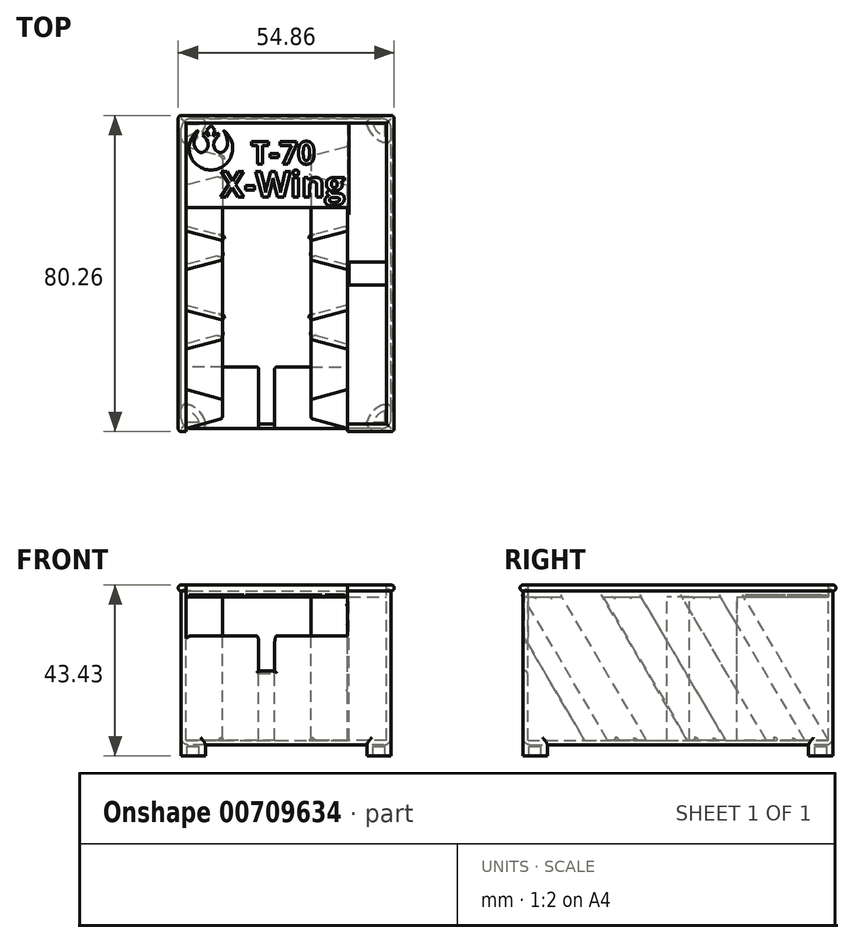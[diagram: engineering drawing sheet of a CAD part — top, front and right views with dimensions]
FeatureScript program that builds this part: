
annotation { "Feature Type Name" : "Feature", "Feature Type Description" : "" }
export const myFeature = defineFeature(function(context is Context, id is Id, definition is map)
    precondition{}
    {
        {
            var Q0;
            Q0=qCreatedBy(makeId("Front.planeOp"),FACE);
            var sketch = newSketch(context, id + "F0", { "sketchPlane" : qUnion([Q0])});
            skLineSegment(sketch, "E0.bottom", {"start": v(26.67, -20.32) * mm, "end": v(-26.67, -20.32) * mm});
            skLineSegment(sketch, "E0.top", {"start": v(26.67, 20.32) * mm, "end": v(-26.67, 20.32) * mm});
            skLineSegment(sketch, "E0.left", {"start": v(26.67, -20.32) * mm, "end": v(26.67, 20.32) * mm});
            skLineSegment(sketch, "E0.right", {"start": v(-26.67, -20.32) * mm, "end": v(-26.67, 20.32) * mm});
            skPoint(sketch, "E0.middle", {"position": v(0, 0) * mm});
            skSolve(sketch);
        }
        {
            var Q0;
            Q0=qSketchRegion(id+"F0",true);
            extrude(context, id + "F1", {"entities" : qUnion([Q0]), "depth" : 78.74 * mm, "offsetDistance" : 25.4 * mm, "symmetric" : true});
        }
        {
            var Q0;
            Q0=makeQuery(id+"F1.opExtrude","SWEPT_FACE",FACE,{"disambiguationData":[OSD([sQuery(id+"F0.wireOp",EDGE,"E0.top")])]});
            shell(context, id + "F2", {"entities" : qUnion([Q0]), "thickness" : 1.2 * mm});
        }
        {
            var Q0;
            {var subQ0=sQuery(id+"F0.wireOp",EDGE,"E0.right");var subQ3=sQuery(id+"F0.wireOp",EDGE,"E0.top");Q0=makeQuery(id+"F15.boolean.opBoolean","SPLIT",EDGE,{"disambiguationData":[TD([makeQuery(id+"F2.opShell","OFFSET_FACE",FACE,{"disambiguationData":[OSD([subQ0])]})])],"derivedFrom":makeQuery(id+"F2.opShell","OFFSET_EDGE",EDGE,{"disambiguationData":[OSD([subQ3]),TDD([makeQuery(id+"F1.opExtrude","CAP_EDGE",EDGE,{"disambiguationData":[OSD([subQ3])],"isStart":false})])]})});}
            var Q1;
            {var subQ0=sQuery(id+"F6.wireOp",EDGE,"E8");var subQ1=sQuery(id+"F0.wireOp",EDGE,"E0.right");var subQ2=sQuery(id+"F0.wireOp",EDGE,"E0.top");var subQ3=makeQuery(id+"F1.opExtrude","CAP_EDGE",EDGE,{"disambiguationData":[OSD([subQ2])],"isStart":false});Q1=makeQuery(id+"F7.boolean.opBoolean","MERGE",EDGE,{"derivedFrom":[subQ3,makeQuery(id+"F7.opSweep","SWEPT_EDGE",EDGE,{"disambiguationData":[OSD([subQ2,subQ1,subQ0]),TDD([subQ3,makeQuery(id+"F6.imprint","INTERSECT",VERTEX,{"derivedFrom":[subQ3,makeQuery(id+"F1.opExtrude","CAP_EDGE",EDGE,{"disambiguationData":[OSD([subQ1])],"isStart":false}),subQ0]})])]})]});}
            cPlane(context, id + "F3", {"entities" : qUnion([Q0, Q1]), "cplaneType" : CPlaneType.LINE_ANGLE, "offset" : 25.4 * mm, "angle" : 30.5 * degree, "oppositeDirection" : true, "width" : 152.4 * mm, "height" : 152.4 * mm});
        }
        {
            var Q0;
            Q0=makeQuery(id+"F2.opShell","OFFSET_FACE",FACE,{"disambiguationData":[OSD([sQuery(id+"F0.wireOp",EDGE,"E0.right")])]});
            var sketch = newSketch(context, id + "F4", { "sketchPlane" : qUnion([Q0])});
            skLineSegment(sketch, "E1.0", {"start": v(38.17, -19.12) * mm, "end": v(38.17, 20.32) * mm});
            skLineSegment(sketch, "E2.1", {"start": v(-38.17, -19.12) * mm, "end": v(38.17, -19.12) * mm});
            skLineSegment(sketch, "E3", {"start": v(38.17, -19.12) * mm, "end": v(-5.73, 55.41) * mm});
            skLineSegment(sketch, "E4.0", {"start": v(-38.17, 20.32) * mm, "end": v(38.17, 20.32) * mm});
            skPoint(sketch, "E5", {"position": v(14.94, 20.32) * mm});
            skSolve(sketch);
        }
        {
            var Q0;
            Q0=qCreatedBy(id+"F3.planeOp",FACE);
            var sketch = newSketch(context, id + "F5", { "sketchPlane" : qUnion([Q0])});
            skPoint(sketch, "E6.0", {"position": v(-25.47, 23.18) * mm});
            skSolve(sketch);
        }
        {
            var Q0;
            Q0=makeQuery(id+"F1.opExtrude","CAP_FACE",FACE,{"disambiguationData":[OSD([sQuery(id+"F0.wireOp",EDGE,"E0.bottom"),sQuery(id+"F0.wireOp",EDGE,"E0.top"),sQuery(id+"F0.wireOp",EDGE,"E0.left"),sQuery(id+"F0.wireOp",EDGE,"E0.right")])],"isStart":false});
            var sketch = newSketch(context, id + "F6", { "sketchPlane" : qUnion([Q0])});
            skArc(sketch, "E7", {"start": v(-122.9, 118.26) * mm, "mid": v(-123.67, 117.5) * mm, "end": v(-122.9, 116.74) * mm});
            skArc(sketch, "E8", {"start": v(-26.67, 20.32) * mm, "mid": v(-27.43, 19.56) * mm, "end": v(-26.67, 18.8) * mm});
            skSolve(sketch);
        }
        {
            var Q0;
            {var subQ0=sQuery(id+"F6.wireOp",EDGE,"E8");Q0=makeQuery(id+"F6.imprint","IMPRINT",FACE,{"disambiguationData":[TD([[makeQuery(id+"F6.imprint","IMPRINT",EDGE,{"derivedFrom":subQ0}),1.0]])]});}
            var Q1;
            Q1=makeQuery(id+"F1.opExtrude","CAP_EDGE",EDGE,{"disambiguationData":[OSD([sQuery(id+"F0.wireOp",EDGE,"E0.top")])],"isStart":false});
            var Q2;
            Q2=makeQuery(id+"F1.opExtrude","SWEPT_EDGE",EDGE,{"disambiguationData":[OSD([sQuery(id+"F0.wireOp",EDGE,"E0.top"),sQuery(id+"F0.wireOp",EDGE,"E0.right")])]});
            var Q3;
            Q3=makeQuery(id+"F1.opExtrude","SWEPT_EDGE",EDGE,{"disambiguationData":[OSD([sQuery(id+"F0.wireOp",EDGE,"E0.top"),sQuery(id+"F0.wireOp",EDGE,"E0.left")])]});
            var Q4;
            Q4=makeQuery(id+"F1.opExtrude","CAP_EDGE",EDGE,{"disambiguationData":[OSD([sQuery(id+"F0.wireOp",EDGE,"E0.top")])],"isStart":true});
            sweep(context, id + "F7", {"operationType" : NewBodyOperationType.ADD, "profiles" : qUnion([Q0]), "path" : qUnion([Q1, Q2, Q3, Q4])});
        }
        {
            var Q0;
            Q0=makeQuery(id+"F1.opExtrude","SWEPT_FACE",FACE,{"disambiguationData":[OSD([sQuery(id+"F0.wireOp",EDGE,"E0.bottom")])]});
            var sketch = newSketch(context, id + "F8", { "sketchPlane" : qUnion([Q0])});
            skLineSegment(sketch, "E9.bottom", {"start": v(26.67, 39.37) * mm, "end": v(21.75, 39.37) * mm});
            skLineSegment(sketch, "E9.left", {"start": v(26.67, 39.37) * mm, "end": v(26.67, 34.45) * mm});
            skPoint(sketch, "E10.newPointA", {"position": v(20.32, 19.05) * mm});
            skArc(sketch, "E11", {"start": v(20.52, 37.78) * mm, "mid": v(22.18, 34.88) * mm, "end": v(25.08, 33.22) * mm});
            skPoint(sketch, "E12.visualSharp", {"position": v(20.32, 39.37) * mm});
            skArc(sketch, "E12.filletArc", {"start": v(21.75, 39.37) * mm, "mid": v(20.75, 38.88) * mm, "end": v(20.52, 37.78) * mm});
            skPoint(sketch, "E13.visualSharp", {"position": v(26.67, 33.02) * mm});
            skArc(sketch, "E13.filletArc", {"start": v(25.08, 33.22) * mm, "mid": v(26.18, 33.45) * mm, "end": v(26.67, 34.45) * mm});
            skArc(sketch, "E14.MirrorCS", {"start": v(-21.75, 39.37) * mm, "mid": v(-20.75, 38.88) * mm, "end": v(-20.52, 37.78) * mm});
            skArc(sketch, "E15.MirrorCS", {"start": v(-20.52, 37.78) * mm, "mid": v(-22.18, 34.88) * mm, "end": v(-25.08, 33.22) * mm});
            skArc(sketch, "E16.MirrorCS", {"start": v(-25.08, 33.22) * mm, "mid": v(-26.18, 33.45) * mm, "end": v(-26.67, 34.45) * mm});
            skLineSegment(sketch, "E17.MirrorCS", {"start": v(-26.67, 39.37) * mm, "end": v(-26.67, 34.45) * mm});
            skLineSegment(sketch, "E18.MirrorCS", {"start": v(-26.67, 39.37) * mm, "end": v(-21.75, 39.37) * mm});
            skArc(sketch, "E19.MirrorCS", {"start": v(-20.52, -37.78) * mm, "mid": v(-22.18, -34.88) * mm, "end": v(-25.08, -33.22) * mm});
            skArc(sketch, "E20.MirrorCS", {"start": v(-21.75, -39.37) * mm, "mid": v(-20.75, -38.88) * mm, "end": v(-20.52, -37.78) * mm});
            skLineSegment(sketch, "E21.MirrorCS", {"start": v(-26.67, -39.37) * mm, "end": v(-21.75, -39.37) * mm});
            skLineSegment(sketch, "E22.MirrorCS", {"start": v(-26.67, -39.37) * mm, "end": v(-26.67, -34.45) * mm});
            skArc(sketch, "E23.MirrorCS", {"start": v(-25.08, -33.22) * mm, "mid": v(-26.18, -33.45) * mm, "end": v(-26.67, -34.45) * mm});
            skArc(sketch, "E24.MirrorCS", {"start": v(21.75, -39.37) * mm, "mid": v(20.75, -38.88) * mm, "end": v(20.52, -37.78) * mm});
            skArc(sketch, "E25.MirrorCS", {"start": v(20.52, -37.78) * mm, "mid": v(22.18, -34.88) * mm, "end": v(25.08, -33.22) * mm});
            skArc(sketch, "E26.MirrorCS", {"start": v(25.08, -33.22) * mm, "mid": v(26.18, -33.45) * mm, "end": v(26.67, -34.45) * mm});
            skLineSegment(sketch, "E27.MirrorCS", {"start": v(26.67, -39.37) * mm, "end": v(26.67, -34.45) * mm});
            skLineSegment(sketch, "E28.MirrorCS", {"start": v(26.67, -39.37) * mm, "end": v(21.75, -39.37) * mm});
            skSolve(sketch);
        }
        {
            var Q0;
            Q0=qSketchRegion(id+"F8",true);
            extrude(context, id + "F9", {"entities" : qUnion([Q0]), "operationType" : NewBodyOperationType.ADD, "depth" : 2.8 * mm, "offsetDistance" : 25.4 * mm});
        }
        {
            var Q0;
            Q0=makeQuery(id+"F9.opExtrude","CAP_FACE",FACE,{"disambiguationData":[OSD([sQuery(id+"F8.wireOp",EDGE,"E15.MirrorCS"),sQuery(id+"F8.wireOp",EDGE,"E16.MirrorCS"),sQuery(id+"F8.wireOp",EDGE,"E17.MirrorCS"),sQuery(id+"F8.wireOp",EDGE,"E14.MirrorCS"),sQuery(id+"F8.wireOp",EDGE,"E18.MirrorCS")])],"isStart":false});
            var Q1;
            Q1=makeQuery(id+"F9.opExtrude","CAP_FACE",FACE,{"disambiguationData":[OSD([sQuery(id+"F8.wireOp",EDGE,"E9.bottom"),sQuery(id+"F8.wireOp",EDGE,"E9.left"),sQuery(id+"F8.wireOp",EDGE,"E11"),sQuery(id+"F8.wireOp",EDGE,"E12.filletArc"),sQuery(id+"F8.wireOp",EDGE,"E13.filletArc")])],"isStart":false});
            var Q2;
            Q2=makeQuery(id+"F9.opExtrude","CAP_FACE",FACE,{"disambiguationData":[OSD([sQuery(id+"F8.wireOp",EDGE,"E24.MirrorCS"),sQuery(id+"F8.wireOp",EDGE,"E25.MirrorCS"),sQuery(id+"F8.wireOp",EDGE,"E26.MirrorCS"),sQuery(id+"F8.wireOp",EDGE,"E27.MirrorCS"),sQuery(id+"F8.wireOp",EDGE,"E28.MirrorCS")])],"isStart":false});
            var Q3;
            Q3=makeQuery(id+"F9.opExtrude","CAP_FACE",FACE,{"disambiguationData":[OSD([sQuery(id+"F8.wireOp",EDGE,"E19.MirrorCS"),sQuery(id+"F8.wireOp",EDGE,"E20.MirrorCS"),sQuery(id+"F8.wireOp",EDGE,"E21.MirrorCS"),sQuery(id+"F8.wireOp",EDGE,"E22.MirrorCS"),sQuery(id+"F8.wireOp",EDGE,"E23.MirrorCS")])],"isStart":false});
            shell(context, id + "F10", {"entities" : qUnion([Q0, Q1, Q2, Q3]), "thickness" : 1.52 * mm});
        }
        {
            var Q0;
            Q0=makeQuery(id+"F7.opSweep","MID_CAP_EDGE",EDGE,{"disambiguationData":[OSD([sQuery(id+"F0.wireOp",EDGE,"E0.top"),sQuery(id+"F0.wireOp",EDGE,"E0.right"),sQuery(id+"F6.wireOp",EDGE,"E8")])],"capPos":1.0});
            var Q1;
            Q1=makeQuery(id+"F7.opSweep","CAP_EDGE",EDGE,{"disambiguationData":[OSD([sQuery(id+"F0.wireOp",EDGE,"E0.top"),sQuery(id+"F0.wireOp",EDGE,"E0.right"),sQuery(id+"F6.wireOp",EDGE,"E8")])],"isStart":true});
            var Q2;
            Q2=makeQuery(id+"F7.opSweep","MID_CAP_EDGE",EDGE,{"disambiguationData":[OSD([sQuery(id+"F0.wireOp",EDGE,"E0.top"),sQuery(id+"F0.wireOp",EDGE,"E0.left"),sQuery(id+"F6.wireOp",EDGE,"E8")])],"capPos":3.0});
            var Q3;
            Q3=makeQuery(id+"F7.opSweep","MID_CAP_EDGE",EDGE,{"disambiguationData":[OSD([sQuery(id+"F0.wireOp",EDGE,"E0.top"),sQuery(id+"F0.wireOp",EDGE,"E0.left"),sQuery(id+"F6.wireOp",EDGE,"E8")])],"capPos":2.0});
            fillet(context, id + "F11", {"entities" : qUnion([Q0, Q1, Q2, Q3]), "radius" : 0.76 * mm, "tangentPropagation" : true, "allowEdgeOverflow" : false});
        }
        {
            var Q0;
            Q0=makeQuery(id+"F9.boolean.opBoolean","MERGE",EDGE,{"derivedFrom":[makeQuery(id+"F1.opExtrude","CAP_EDGE",EDGE,{"disambiguationData":[OSD([sQuery(id+"F0.wireOp",EDGE,"E0.right")])],"isStart":false}),makeQuery(id+"F9.opExtrude","SWEPT_EDGE",EDGE,{"disambiguationData":[OSD([sQuery(id+"F8.wireOp",EDGE,"E17.MirrorCS"),sQuery(id+"F8.wireOp",EDGE,"E18.MirrorCS")])]})]});
            var Q1;
            Q1=makeQuery(id+"F9.boolean.opBoolean","MERGE",EDGE,{"derivedFrom":[makeQuery(id+"F1.opExtrude","CAP_EDGE",EDGE,{"disambiguationData":[OSD([sQuery(id+"F0.wireOp",EDGE,"E0.left")])],"isStart":false}),makeQuery(id+"F9.opExtrude","SWEPT_EDGE",EDGE,{"disambiguationData":[OSD([sQuery(id+"F8.wireOp",EDGE,"E9.bottom"),sQuery(id+"F8.wireOp",EDGE,"E9.left")])]})]});
            var Q2;
            Q2=makeQuery(id+"F9.boolean.opBoolean","MERGE",EDGE,{"derivedFrom":[makeQuery(id+"F1.opExtrude","CAP_EDGE",EDGE,{"disambiguationData":[OSD([sQuery(id+"F0.wireOp",EDGE,"E0.left")])],"isStart":true}),makeQuery(id+"F9.opExtrude","SWEPT_EDGE",EDGE,{"disambiguationData":[OSD([sQuery(id+"F8.wireOp",EDGE,"E27.MirrorCS"),sQuery(id+"F8.wireOp",EDGE,"E28.MirrorCS")])]})]});
            var Q3;
            Q3=makeQuery(id+"F9.boolean.opBoolean","MERGE",EDGE,{"derivedFrom":[makeQuery(id+"F1.opExtrude","CAP_EDGE",EDGE,{"disambiguationData":[OSD([sQuery(id+"F0.wireOp",EDGE,"E0.right")])],"isStart":true}),makeQuery(id+"F9.opExtrude","SWEPT_EDGE",EDGE,{"disambiguationData":[OSD([sQuery(id+"F8.wireOp",EDGE,"E21.MirrorCS"),sQuery(id+"F8.wireOp",EDGE,"E22.MirrorCS")])]})]});
            fillet(context, id + "F12", {"entities" : qUnion([Q0, Q1, Q2, Q3]), "radius" : 2.54 * mm, "tangentPropagation" : true, "allowEdgeOverflow" : false});
        }
        {
            var Q0;
            Q0=makeQuery(id+"F1.opExtrude","SWEPT_EDGE",EDGE,{"disambiguationData":[OSD([sQuery(id+"F0.wireOp",EDGE,"E0.bottom"),sQuery(id+"F0.wireOp",EDGE,"E0.right")])]});
            var Q1;
            Q1=makeQuery(id+"F1.opExtrude","CAP_EDGE",EDGE,{"disambiguationData":[OSD([sQuery(id+"F0.wireOp",EDGE,"E0.bottom")])],"isStart":false});
            var Q2;
            Q2=makeQuery(id+"F1.opExtrude","SWEPT_EDGE",EDGE,{"disambiguationData":[OSD([sQuery(id+"F0.wireOp",EDGE,"E0.bottom"),sQuery(id+"F0.wireOp",EDGE,"E0.left")])]});
            var Q3;
            Q3=makeQuery(id+"F1.opExtrude","CAP_EDGE",EDGE,{"disambiguationData":[OSD([sQuery(id+"F0.wireOp",EDGE,"E0.bottom")])],"isStart":true});
            fillet(context, id + "F13", {"entities" : qUnion([Q0, Q1, Q2, Q3]), "radius" : 1.9 * mm, "tangentPropagation" : true, "allowEdgeOverflow" : false});
        }
        {
            var Q0;
            Q0=makeQuery(id+"F23.boolean.opBoolean","MERGE",FACE,{"derivedFrom":[makeQuery(id+"F1.opExtrude","SWEPT_FACE",FACE,{"disambiguationData":[OSD([sQuery(id+"F0.wireOp",EDGE,"E0.top")])]}),makeQuery(id+"F23.opExtrude","CAP_FACE",FACE,{"disambiguationData":[OSD([sQuery(id+"F22.wireOp",EDGE,"CeT5EqMD-vzeh-J7pB-LkoM-5uFaC58c3kCY.bottom"),sQuery(id+"F22.wireOp",EDGE,"CeT5EqMD-vzeh-J7pB-LkoM-5uFaC58c3kCY.top"),sQuery(id+"F22.wireOp",EDGE,"CeT5EqMD-vzeh-J7pB-LkoM-5uFaC58c3kCY.left"),sQuery(id+"F22.wireOp",EDGE,"CeT5EqMD-vzeh-J7pB-LkoM-5uFaC58c3kCY.right")])],"isStart":true})]});
            var sketch = newSketch(context, id + "F14", { "sketchPlane" : qUnion([Q0])});
            skLineSegment(sketch, "E29.bottom", {"start": v(25.47, 38.17) * mm, "end": v(15.93, 38.17) * mm});
            skLineSegment(sketch, "E29.top", {"start": v(25.47, 2.86) * mm, "end": v(15.93, 2.86) * mm});
            skLineSegment(sketch, "E29.left", {"start": v(25.47, 38.17) * mm, "end": v(25.47, 2.86) * mm});
            skLineSegment(sketch, "E29.right", {"start": v(15.93, 38.17) * mm, "end": v(15.93, 2.86) * mm});
            skLineSegment(sketch, "E30.bottom", {"start": v(25.47, -38.17) * mm, "end": v(15.93, -38.17) * mm});
            skLineSegment(sketch, "E30.top", {"start": v(25.47, -2.86) * mm, "end": v(15.93, -2.86) * mm});
            skLineSegment(sketch, "E30.left", {"start": v(25.47, -38.17) * mm, "end": v(25.47, -2.86) * mm});
            skLineSegment(sketch, "E30.right", {"start": v(15.93, -38.17) * mm, "end": v(15.93, -2.86) * mm});
            skLineSegment(sketch, "E31.bottom", {"start": v(25.47, 38.17) * mm, "end": v(-25.47, 38.17) * mm});
            skLineSegment(sketch, "E31.top", {"start": v(25.47, -38.17) * mm, "end": v(-25.47, -38.17) * mm});
            skLineSegment(sketch, "E31.left", {"start": v(25.47, 38.17) * mm, "end": v(25.47, -38.17) * mm});
            skLineSegment(sketch, "E31.right", {"start": v(-25.47, 38.17) * mm, "end": v(-25.47, -38.17) * mm});
            skLineSegment(sketch, "E32", {"start": v(15.93, -38.17) * mm, "end": v(15.93, -38.17) * mm});
            skLineSegment(sketch, "E33", {"start": v(15.93, -38.17) * mm, "end": v(15.93, 38.17) * mm});
            skLineSegment(sketch, "E34.0", {"start": v(-25.47, 38.17) * mm, "end": v(-25.47, -5.73) * mm});
            skPoint(sketch, "E35.0", {"position": v(-25.47, 14.94) * mm});
            skLineSegment(sketch, "E36", {"start": v(-25.47, 14.94) * mm, "end": v(15.93, 14.94) * mm});
            skSolve(sketch);
        }
        {
            var Q0;
            {var subQ3=sQuery(id+"F14.wireOp",EDGE,"E29.top");Q0=makeQuery(id+"F14.imprint","IMPRINT",FACE,{"disambiguationData":[TD([[makeQuery(id+"F14.imprint","IMPRINT",EDGE,{"derivedFrom":subQ3}),1.0]])]});}
            var Q1;
            {var subQ5=sQuery(id+"F14.wireOp",EDGE,"E36");Q1=makeQuery(id+"F14.imprint","IMPRINT",FACE,{"disambiguationData":[TD([[makeQuery(id+"F14.imprint","IMPRINT",EDGE,{"derivedFrom":subQ5}),1.0]])]});}
            var Q2;
            Q2=makeQuery(id+"F2.opShell","OFFSET_FACE",FACE,{"disambiguationData":[OSD([sQuery(id+"F0.wireOp",EDGE,"E0.bottom")])]});
            extrude(context, id + "F15", {"entities" : qUnion([Q0, Q1]), "operationType" : NewBodyOperationType.ADD, "endBound" : BoundingType.UP_TO_SURFACE, "oppositeDirection" : true, "depth" : 25.4 * mm, "endBoundEntityFace" : qUnion([Q2]), "offsetDistance" : 25.4 * mm});
        }
        {
            var Q0;
            Q0=qCreatedBy(id+"F3.planeOp",FACE);
            var sketch = newSketch(context, id + "F16", { "sketchPlane" : qUnion([Q0])});
            skLineSegment(sketch, "E37.0", {"start": v(-25.47, -16.63) * mm, "end": v(-25.47, -7.74) * mm});
            skLineSegment(sketch, "E38", {"start": v(-25.47, 23.18) * mm, "end": v(-4.77, 23.18) * mm});
            skPoint(sketch, "E39.0", {"position": v(-25.47, 23.18) * mm});
            skLineSegment(sketch, "E40", {"start": v(-25.47, 23.18) * mm, "end": v(-25.47, 18.1) * mm});
            skLineSegment(sketch, "E41", {"start": v(-25.47, 18.1) * mm, "end": v(-16.19, 15.96) * mm});
            skLineSegment(sketch, "E42", {"start": v(-16.19, 15.96) * mm, "end": v(-16.19, 11.77) * mm});
            skLineSegment(sketch, "E43", {"start": v(-16.19, 11.77) * mm, "end": v(-25.47, 9.63) * mm});
            skLineSegment(sketch, "E44", {"start": v(-25.47, 9.63) * mm, "end": v(-25.47, 0.74) * mm});
            skLineSegment(sketch, "E45", {"start": v(-25.47, 0.74) * mm, "end": v(-16.19, -1.4) * mm});
            skLineSegment(sketch, "E46", {"start": v(-16.19, -1.4) * mm, "end": v(-16.19, -5.6) * mm});
            skLineSegment(sketch, "E47", {"start": v(-16.19, -5.6) * mm, "end": v(-25.47, -7.74) * mm});
            skLineSegment(sketch, "E48", {"start": v(-25.47, -7.74) * mm, "end": v(-25.47, -16.63) * mm});
            skLineSegment(sketch, "E49", {"start": v(-25.47, -16.63) * mm, "end": v(-16.19, -18.77) * mm});
            skLineSegment(sketch, "E50", {"start": v(-16.19, -18.77) * mm, "end": v(-16.19, -22.96) * mm});
            skLineSegment(sketch, "E51", {"start": v(-16.19, -22.96) * mm, "end": v(-25.47, -25.1) * mm});
            skLineSegment(sketch, "E52", {"start": v(-25.47, -25.1) * mm, "end": v(-25.47, -30.18) * mm});
            skLineSegment(sketch, "E53", {"start": v(-25.47, -30.18) * mm, "end": v(-7, -30.18) * mm});
            skLineSegment(sketch, "E54", {"start": v(-7, -30.18) * mm, "end": v(-7, -34) * mm});
            skLineSegment(sketch, "E55", {"start": v(-7, -34) * mm, "end": v(-4.77, -34) * mm});
            skLineSegment(sketch, "E56.trimOffspring", {"start": v(-25.47, 0.74) * mm, "end": v(-25.47, 9.63) * mm});
            skLineSegment(sketch, "E57.trimOffspring", {"start": v(-25.47, 18.1) * mm, "end": v(-25.47, 23.18) * mm});
            skPoint(sketch, "E58.orphan", {"position": v(-25.47, -22.58) * mm});
            skLineSegment(sketch, "E59", {"start": v(-4.95, -94.16) * mm, "end": v(-4.95, 57.75) * mm});
            skLineSegment(sketch, "E60.MirrorCS", {"start": v(15.56, 23.18) * mm, "end": v(15.56, 18.1) * mm});
            skLineSegment(sketch, "E61.MirrorCS", {"start": v(6.28, -1.4) * mm, "end": v(6.28, -5.6) * mm});
            skLineSegment(sketch, "E62.MirrorCS", {"start": v(-2.91, -34) * mm, "end": v(-5.14, -34) * mm});
            skLineSegment(sketch, "E63.MirrorCS", {"start": v(15.56, 18.1) * mm, "end": v(15.56, 23.18) * mm});
            skLineSegment(sketch, "E64.MirrorCS", {"start": v(6.28, 15.96) * mm, "end": v(6.28, 11.77) * mm});
            skLineSegment(sketch, "E65.MirrorCS", {"start": v(6.28, -18.77) * mm, "end": v(6.28, -22.96) * mm});
            skLineSegment(sketch, "E66.MirrorCS", {"start": v(15.56, -16.63) * mm, "end": v(15.56, -7.74) * mm});
            skLineSegment(sketch, "E67.MirrorCS", {"start": v(-2.91, -30.18) * mm, "end": v(-2.91, -34) * mm});
            skLineSegment(sketch, "E68.MirrorCS", {"start": v(15.56, 18.1) * mm, "end": v(6.28, 15.96) * mm});
            skLineSegment(sketch, "E69.MirrorCS", {"start": v(6.28, 11.77) * mm, "end": v(15.56, 9.63) * mm});
            skLineSegment(sketch, "E70.MirrorCS", {"start": v(15.56, 0.74) * mm, "end": v(15.56, 9.63) * mm});
            skLineSegment(sketch, "E71.MirrorCS", {"start": v(15.56, -7.74) * mm, "end": v(15.56, -16.63) * mm});
            skLineSegment(sketch, "E72.MirrorCS", {"start": v(6.28, -5.6) * mm, "end": v(15.56, -7.74) * mm});
            skLineSegment(sketch, "E73.MirrorCS", {"start": v(6.28, -22.96) * mm, "end": v(15.56, -25.1) * mm});
            skPoint(sketch, "E74.MirrorP", {"position": v(15.56, -22.58) * mm});
            skLineSegment(sketch, "E75.MirrorCS", {"start": v(15.56, -16.63) * mm, "end": v(6.28, -18.77) * mm});
            skLineSegment(sketch, "E76.MirrorCS", {"start": v(15.56, -25.1) * mm, "end": v(15.56, -30.18) * mm});
            skLineSegment(sketch, "E77.MirrorCS", {"start": v(15.56, -30.18) * mm, "end": v(-2.91, -30.18) * mm});
            skLineSegment(sketch, "E78.MirrorCS", {"start": v(15.56, 0.74) * mm, "end": v(6.28, -1.4) * mm});
            skLineSegment(sketch, "E79.MirrorCS", {"start": v(15.56, 23.18) * mm, "end": v(-5.14, 23.18) * mm});
            skLineSegment(sketch, "E80.MirrorCS", {"start": v(15.56, 9.63) * mm, "end": v(15.56, 0.74) * mm});
            skPoint(sketch, "E81.MirrorP", {"position": v(15.56, 23.18) * mm});
            skLineSegment(sketch, "E82.bottom", {"start": v(-25.47, 23.18) * mm, "end": v(15.56, 23.18) * mm});
            skLineSegment(sketch, "E82.top", {"start": v(-25.47, -30.18) * mm, "end": v(15.56, -30.18) * mm});
            skLineSegment(sketch, "E82.left", {"start": v(-25.47, 23.18) * mm, "end": v(-25.47, -30.18) * mm});
            skLineSegment(sketch, "E82.right", {"start": v(15.56, 23.18) * mm, "end": v(15.56, -30.18) * mm});
            skSolve(sketch);
        }
        {
            var Q0;
            {var subQ0=sQuery(id+"F16.wireOp",EDGE,"E41");Q0=makeQuery(id+"F16.imprint","IMPRINT",FACE,{"disambiguationData":[TD([[makeQuery(id+"F16.imprint","IMPRINT",EDGE,{"derivedFrom":subQ0}),-1.0]])]});}
            var Q1;
            {var subQ0=sQuery(id+"F16.wireOp",EDGE,"E45");Q1=makeQuery(id+"F16.imprint","IMPRINT",FACE,{"disambiguationData":[TD([[makeQuery(id+"F16.imprint","IMPRINT",EDGE,{"derivedFrom":subQ0}),-1.0]])]});}
            var Q2;
            {var subQ0=sQuery(id+"F16.wireOp",EDGE,"E49");Q2=makeQuery(id+"F16.imprint","IMPRINT",FACE,{"disambiguationData":[TD([[makeQuery(id+"F16.imprint","IMPRINT",EDGE,{"derivedFrom":subQ0}),-1.0]])]});}
            var Q3;
            Q3=makeQuery(id+"F16.imprint","IMPRINT",FACE,{"disambiguationData":[TD([[makeQuery(id+"F16.imprint","IMPRINT",EDGE,{"derivedFrom":sQuery(id+"F16.wireOp",EDGE,"E65.MirrorCS")}),1.0]])]});
            var Q4;
            Q4=makeQuery(id+"F16.imprint","IMPRINT",FACE,{"disambiguationData":[TD([[makeQuery(id+"F16.imprint","IMPRINT",EDGE,{"derivedFrom":sQuery(id+"F16.wireOp",EDGE,"E61.MirrorCS")}),1.0]])]});
            var Q5;
            Q5=makeQuery(id+"F16.imprint","IMPRINT",FACE,{"disambiguationData":[TD([[makeQuery(id+"F16.imprint","IMPRINT",EDGE,{"derivedFrom":sQuery(id+"F16.wireOp",EDGE,"E64.MirrorCS")}),1.0]])]});
            extrude(context, id + "F17", {"entities" : qUnion([Q0, Q1, Q2, Q3, Q4, Q5]), "operationType" : NewBodyOperationType.ADD, "endBound" : BoundingType.UP_TO_NEXT, "oppositeDirection" : true, "depth" : 25.4 * mm, "offsetDistance" : 25.4 * mm});
        }
        {
            var Q0;
            {var subQ2=sQuery(id+"F16.wireOp",EDGE,"E41");Q0=makeQuery(id+"F16.imprint","IMPRINT",FACE,{"disambiguationData":[TD([[makeQuery(id+"F16.imprint","IMPRINT",EDGE,{"derivedFrom":subQ2}),1.0]])]});}
            var Q1;
            Q1=makeQuery(id+"F16.imprint","IMPRINT",FACE,{"disambiguationData":[TD([[makeQuery(id+"F16.imprint","IMPRINT",EDGE,{"derivedFrom":sQuery(id+"F16.wireOp",EDGE,"E61.MirrorCS")}),-1.0]])]});
            var Q2;
            {var subQ0=sQuery(id+"F16.wireOp",EDGE,"E62.MirrorCS");Q2=makeQuery(id+"F16.imprint","IMPRINT",FACE,{"disambiguationData":[TD([[makeQuery(id+"F16.imprint","IMPRINT",EDGE,{"derivedFrom":subQ0}),-1.0]])]});}
            var Q3;
            {var subQ0=sQuery(id+"F16.wireOp",EDGE,"E54");Q3=makeQuery(id+"F16.imprint","IMPRINT",FACE,{"disambiguationData":[TD([[makeQuery(id+"F16.imprint","IMPRINT",EDGE,{"derivedFrom":subQ0}),1.0]])]});}
            var Q4;
            {var subQ0=sQuery(id+"F0.wireOp",EDGE,"E0.right");var subQ3=sQuery(id+"F0.wireOp",EDGE,"E0.bottom");Q4=makeQuery(id+"F15.boolean.opBoolean","SPLIT",FACE,{"disambiguationData":[TD([makeQuery(id+"F2.opShell","OFFSET_FACE",FACE,{"disambiguationData":[OSD([subQ0])]})])],"derivedFrom":makeQuery(id+"F2.opShell","OFFSET_FACE",FACE,{"disambiguationData":[OSD([subQ3])]})});}
            extrude(context, id + "F18", {"entities" : qUnion([Q0, Q1, Q2, Q3]), "operationType" : NewBodyOperationType.REMOVE, "endBound" : BoundingType.UP_TO_SURFACE, "oppositeDirection" : true, "depth" : 25.4 * mm, "endBoundEntityFace" : qUnion([Q4]), "offsetDistance" : 25.4 * mm});
        }
        {
            var Q0;
            {var subQ2=sQuery(id+"F16.wireOp",EDGE,"E41");Q0=makeQuery(id+"F16.imprint","IMPRINT",FACE,{"disambiguationData":[TD([[makeQuery(id+"F16.imprint","IMPRINT",EDGE,{"derivedFrom":subQ2}),1.0]])]});}
            var Q1;
            Q1=makeQuery(id+"F16.imprint","IMPRINT",FACE,{"disambiguationData":[TD([[makeQuery(id+"F16.imprint","IMPRINT",EDGE,{"derivedFrom":sQuery(id+"F16.wireOp",EDGE,"E61.MirrorCS")}),-1.0]])]});
            var Q2;
            {var subQ0=sQuery(id+"F16.wireOp",EDGE,"E62.MirrorCS");Q2=makeQuery(id+"F16.imprint","IMPRINT",FACE,{"disambiguationData":[TD([[makeQuery(id+"F16.imprint","IMPRINT",EDGE,{"derivedFrom":subQ0}),-1.0]])]});}
            var Q3;
            {var subQ0=sQuery(id+"F16.wireOp",EDGE,"E54");Q3=makeQuery(id+"F16.imprint","IMPRINT",FACE,{"disambiguationData":[TD([[makeQuery(id+"F16.imprint","IMPRINT",EDGE,{"derivedFrom":subQ0}),1.0]])]});}
            extrude(context, id + "F19", {"entities" : qUnion([Q0, Q1, Q2, Q3]), "operationType" : NewBodyOperationType.REMOVE, "depth" : 25.4 * mm, "offsetDistance" : 25.4 * mm});
        }
        {
            var Q0;
            Q0=makeQuery(id+"F15.boolean.opBoolean","MERGE",FACE,{"derivedFrom":[makeQuery(id+"F1.opExtrude","SWEPT_FACE",FACE,{"disambiguationData":[OSD([sQuery(id+"F0.wireOp",EDGE,"E0.top")])]}),makeQuery(id+"F15.opExtrude","CAP_FACE",FACE,{"disambiguationData":[OSD([sQuery(id+"F14.wireOp",EDGE,"hc8ozTBv-Tm9a-kJ22-CKKE-tXYxZ9j7C9O8.right"),sQuery(id+"F14.wireOp",EDGE,"axl2OUU4-iXIp-PN5l-KddX-B3juGezwyh9M"),sQuery(id+"F14.wireOp",EDGE,"pRjz3Pr6-j7dV-o5ry-EZdA-GTtMzoIt95sS"),sQuery(id+"F14.wireOp",EDGE,"v856Wygs-yZXH-i2VT-3ghV-dVD4C32cBXVV"),sQuery(id+"F14.wireOp",EDGE,"USvI0tPl-EBY3-tKBE-jOEe-J8Xq5xi1xeiV"),sQuery(id+"F14.wireOp",EDGE,"k8kRmxcm-2nWE-OpHm-94qM-GIo2QhKUa4bU"),sQuery(id+"F14.wireOp",EDGE,"X1O9FMfb-903Z-7eNO-K9uC-zuuZ2nm40ufy"),sQuery(id+"F14.wireOp",EDGE,"r2gNmgJv-KwMP-WI78-23uA-wNcYgOeBLYQq"),sQuery(id+"F14.wireOp",EDGE,"vQvzNP03-p6BG-Xv0D-D307-GviAW00GZ98y"),sQuery(id+"F14.wireOp",EDGE,"9BoKh5av-tXag-cxfd-tblm-Vw8L67vS9qZj")])],"isStart":true})]});
            var sketch = newSketch(context, id + "F20", { "sketchPlane" : qUnion([Q0])});
            skPoint(sketch, "E83.0", {"position": v(-26.67, 39.37) * mm});
            skPoint(sketch, "E84.0", {"position": v(26.67, -39.37) * mm});
            skLineSegment(sketch, "E85.0", {"start": v(25.47, 38.17) * mm, "end": v(-25.47, 38.17) * mm});
            skLineSegment(sketch, "E86.0", {"start": v(-25.47, 32.27) * mm, "end": v(-25.47, 38.17) * mm});
            skLineSegment(sketch, "E86.1", {"start": v(25.47, 2.86) * mm, "end": v(25.47, 38.17) * mm});
            skLineSegment(sketch, "E86.2", {"start": v(25.47, -38.17) * mm, "end": v(15.56, -38.17) * mm});
            skLineSegment(sketch, "E87.0", {"start": v(15.56, -38.17) * mm, "end": v(15.56, -39.37) * mm});
            skLineSegment(sketch, "E88", {"start": v(-25.47, 32.27) * mm, "end": v(-25.47, -38.17) * mm});
            skLineSegment(sketch, "E89", {"start": v(-25.47, -38.17) * mm, "end": v(-25.47, -58.17) * mm});
            skLineSegment(sketch, "E90", {"start": v(-25.47, -58.17) * mm, "end": v(15.56, -58.17) * mm});
            skLineSegment(sketch, "E91", {"start": v(15.56, -58.17) * mm, "end": v(15.56, -39.37) * mm});
            skLineSegment(sketch, "E92", {"start": v(25.47, 2.86) * mm, "end": v(25.47, -38.17) * mm});
            skSolve(sketch);
        }
        {
            var Q0;
            Q0=qSketchRegion(id+"F20",true);
            extrude(context, id + "F21", {"entities" : qUnion([Q0]), "operationType" : NewBodyOperationType.REMOVE, "depth" : 40 * mm, "offsetDistance" : 25.4 * mm, "hasSecondDirection" : true, "secondDirectionOppositeDirection" : true, "secondDirectionDepth" : 3 * mm});
        }
        {
            var Q0;
            Q0=makeQuery(id+"F9.boolean.opBoolean","MERGE",FACE,{"derivedFrom":[makeQuery(id+"F1.opExtrude","SWEPT_FACE",FACE,{"disambiguationData":[OSD([sQuery(id+"F0.wireOp",EDGE,"E0.left")])]}),makeQuery(id+"F9.opExtrude","SWEPT_FACE",FACE,{"disambiguationData":[OSD([sQuery(id+"F8.wireOp",EDGE,"E9.left")])]}),makeQuery(id+"F9.opExtrude","SWEPT_FACE",FACE,{"disambiguationData":[OSD([sQuery(id+"F8.wireOp",EDGE,"E27.MirrorCS")])]})]});
            var sketch = newSketch(context, id + "F22", { "sketchPlane" : qUnion([Q0])});
            skLineSegment(sketch, "E93.0", {"start": v(-39.37, -23.11) * mm, "end": v(-39.37, 18.8) * mm});
            skArc(sketch, "E93.1", {"start": v(-39.37, 18.8) * mm, "mid": v(-40.13, 19.56) * mm, "end": v(-39.37, 20.32) * mm});
            skLineSegment(sketch, "E94", {"start": v(-39.37, 20.32) * mm, "end": v(-45.72, 20.32) * mm});
            skLineSegment(sketch, "E95", {"start": v(-45.72, 20.32) * mm, "end": v(-45.72, -23.11) * mm});
            skLineSegment(sketch, "E96", {"start": v(-45.72, -23.11) * mm, "end": v(-39.37, -23.11) * mm});
            skSolve(sketch);
        }
        {
            var Q0;
            Q0=qSketchRegion(id+"F22",true);
            extrude(context, id + "F23", {"entities" : qUnion([Q0]), "operationType" : NewBodyOperationType.REMOVE, "oppositeDirection" : true, "depth" : 152.4 * mm, "offsetDistance" : 25.4 * mm});
        }
        {
            var Q0;
            {var subQ2=sQuery(id+"F16.wireOp",EDGE,"E73.MirrorCS");var subQ5=sQuery(id+"F0.wireOp",EDGE,"E0.top");var subQ6=sQuery(id+"F16.wireOp",EDGE,"E82.right");Q0=makeQuery(id+"F17.boolean.opBoolean","SPLIT",FACE,{"disambiguationData":[TD([makeQuery(id+"F1.opExtrude","SWEPT_FACE",FACE,{"disambiguationData":[OSD([subQ5])]})])],"derivedFrom":makeQuery(id+"F17.opExtrude","SWEPT_FACE",FACE,{"disambiguationData":[OSD([subQ6]),TDD([makeQuery(id+"F16.imprint","IMPRINT",EDGE,{"disambiguationData":[TD([[makeQuery(id+"F16.imprint","INTERSECT",VERTEX,{"derivedFrom":[subQ2,subQ6]}),1.0]])],"derivedFrom":subQ6})])]})});}
            var sketch = newSketch(context, id + "F24", { "sketchPlane" : qUnion([Q0])});
            skLineSegment(sketch, "E97.0", {"start": v(-38.17, 5.33) * mm, "end": v(-39.37, 7.36) * mm});
            skLineSegment(sketch, "E98.0", {"start": v(-38.17, -19.12) * mm, "end": v(-38.17, 20.32) * mm});
            skLineSegment(sketch, "E99.0", {"start": v(-38.17, -19.12) * mm, "end": v(-2.86, -19.12) * mm});
            skLineSegment(sketch, "E100", {"start": v(-39.37, 7.36) * mm, "end": v(-21.32, -23.28) * mm});
            skSolve(sketch);
        }
        {
            var Q0;
            {var subQ0=sQuery(id+"F24.wireOp",EDGE,"E99.0");var subQ1=sQuery(id+"F24.wireOp",EDGE,"E98.0");var subQ2=makeQuery(id+"F24.imprint","INTERSECT",VERTEX,{"derivedFrom":[subQ1,subQ0]});Q0=makeQuery(id+"F24.imprint","IMPRINT",FACE,{"disambiguationData":[TD([[makeQuery(id+"F24.imprint","IMPRINT",EDGE,{"disambiguationData":[TD([[subQ2,-1.0]])],"derivedFrom":subQ1}),-1.0]])]});}
            var Q1;
            {var subQ0=sQuery(id+"F0.wireOp",EDGE,"E0.right");var subQ1=sQuery(id+"F0.wireOp",EDGE,"E0.left");var subQ2=sQuery(id+"F0.wireOp",EDGE,"E0.top");var subQ3=sQuery(id+"F0.wireOp",EDGE,"E0.bottom");Q1=makeQuery(id+"F18.boolean.opBoolean","INTERSECT",VERTEX,{"derivedFrom":[makeQuery(id+"F2.opShell","OFFSET_FACE",FACE,{"disambiguationData":[OSD([subQ3,subQ2,subQ1,subQ0]),TDD([makeQuery(id+"F1.opExtrude","CAP_FACE",FACE,{"disambiguationData":[OSD([subQ3,subQ2,subQ1,subQ0])],"isStart":false})])]}),makeQuery(id+"F18.opExtrude","SWEPT_FACE",FACE,{"disambiguationData":[OSD([sQuery(id+"F16.wireOp",EDGE,"E55"),sQuery(id+"F16.wireOp",EDGE,"E62.MirrorCS")])]}),makeQuery(id+"F18.opExtrude","SWEPT_FACE",FACE,{"disambiguationData":[OSD([sQuery(id+"F16.wireOp",EDGE,"E67.MirrorCS")])]})]});}
            extrude(context, id + "F25", {"entities" : qUnion([Q0]), "operationType" : NewBodyOperationType.ADD, "endBound" : BoundingType.UP_TO_VERTEX, "oppositeDirection" : true, "depth" : 25.4 * mm, "endBoundEntityVertex" : qUnion([Q1]), "offsetDistance" : 25.4 * mm});
        }
        {
            var Q0;
            {var subQ0=sQuery(id+"F16.wireOp",EDGE,"E82.left");var subQ1=sQuery(id+"F16.wireOp",EDGE,"E51");var subQ3=sQuery(id+"F0.wireOp",EDGE,"E0.right");Q0=makeQuery(id+"F18.boolean.opBoolean","MERGE",FACE,{"derivedFrom":[makeQuery(id+"F17.boolean.opBoolean","SPLIT",FACE,{"disambiguationData":[TD([makeQuery(id+"F17.opExtrude","SWEPT_FACE",FACE,{"disambiguationData":[OSD([subQ1])]})])],"derivedFrom":makeQuery(id+"F2.opShell","OFFSET_FACE",FACE,{"disambiguationData":[OSD([subQ3])]})}),makeQuery(id+"F18.opExtrude","SWEPT_FACE",FACE,{"disambiguationData":[OSD([subQ0]),TDD([makeQuery(id+"F16.imprint","IMPRINT",EDGE,{"disambiguationData":[TD([[makeQuery(id+"F16.imprint","INTERSECT",VERTEX,{"derivedFrom":[subQ1,subQ0]}),-1.0]])],"derivedFrom":subQ0})])]})]});}
            var sketch = newSketch(context, id + "F26", { "sketchPlane" : qUnion([Q0])});
            skLineSegment(sketch, "E101.0", {"start": v(-38.17, 5.33) * mm, "end": v(-38.99, 6.72) * mm});
            skLineSegment(sketch, "E102.0", {"start": v(-38.17, -19.12) * mm, "end": v(-38.17, 5.33) * mm});
            skLineSegment(sketch, "E103.0", {"start": v(-38.17, -19.12) * mm, "end": v(-17.87, -19.12) * mm});
            skLineSegment(sketch, "E104", {"start": v(-38.99, 6.72) * mm, "end": v(-21.4, -23.15) * mm});
            skSolve(sketch);
        }
        {
            var Q0;
            {var subQ0=sQuery(id+"F26.wireOp",EDGE,"E102.0");Q0=makeQuery(id+"F26.imprint","IMPRINT",FACE,{"disambiguationData":[TD([[makeQuery(id+"F26.imprint","IMPRINT",EDGE,{"derivedFrom":subQ0}),-1.0]])]});}
            var Q1;
            {var subQ0=sQuery(id+"F0.wireOp",EDGE,"E0.right");var subQ1=sQuery(id+"F0.wireOp",EDGE,"E0.left");var subQ2=sQuery(id+"F0.wireOp",EDGE,"E0.top");var subQ3=sQuery(id+"F0.wireOp",EDGE,"E0.bottom");Q1=makeQuery(id+"F18.boolean.opBoolean","INTERSECT",VERTEX,{"derivedFrom":[makeQuery(id+"F2.opShell","OFFSET_FACE",FACE,{"disambiguationData":[OSD([subQ3,subQ2,subQ1,subQ0]),TDD([makeQuery(id+"F1.opExtrude","CAP_FACE",FACE,{"disambiguationData":[OSD([subQ3,subQ2,subQ1,subQ0])],"isStart":false})])]}),makeQuery(id+"F18.opExtrude","SWEPT_FACE",FACE,{"disambiguationData":[OSD([sQuery(id+"F16.wireOp",EDGE,"E54")])]}),makeQuery(id+"F18.opExtrude","SWEPT_FACE",FACE,{"disambiguationData":[OSD([sQuery(id+"F16.wireOp",EDGE,"E55"),sQuery(id+"F16.wireOp",EDGE,"E62.MirrorCS")])]})]});}
            extrude(context, id + "F27", {"entities" : qUnion([Q0]), "operationType" : NewBodyOperationType.ADD, "endBound" : BoundingType.UP_TO_VERTEX, "depth" : 25.4 * mm, "endBoundEntityVertex" : qUnion([Q1]), "offsetDistance" : 25.4 * mm});
        }
        {
            var Q0;
            {var subQ0=sQuery(id+"F16.wireOp",EDGE,"E42");Q0=makeQuery(id+"F18.boolean.opBoolean","MERGE",FACE,{"derivedFrom":[makeQuery(id+"F17.opExtrude","SWEPT_FACE",FACE,{"disambiguationData":[OSD([subQ0])]}),makeQuery(id+"F18.opExtrude","SWEPT_FACE",FACE,{"disambiguationData":[OSD([subQ0])]})]});}
            var Q1;
            Q1=makeQuery(id+"F17.opExtrude","SWEPT_FACE",FACE,{"disambiguationData":[OSD([sQuery(id+"F16.wireOp",EDGE,"E46")])]});
            var Q2;
            {var subQ0=sQuery(id+"F16.wireOp",EDGE,"E50");Q2=makeQuery(id+"F18.boolean.opBoolean","MERGE",FACE,{"derivedFrom":[makeQuery(id+"F17.opExtrude","SWEPT_FACE",FACE,{"disambiguationData":[OSD([subQ0])]}),makeQuery(id+"F18.opExtrude","SWEPT_FACE",FACE,{"disambiguationData":[OSD([subQ0])]})]});}
            var Q3;
            {var subQ0=sQuery(id+"F16.wireOp",EDGE,"E64.MirrorCS");Q3=makeQuery(id+"F18.boolean.opBoolean","MERGE",FACE,{"derivedFrom":[makeQuery(id+"F17.opExtrude","SWEPT_FACE",FACE,{"disambiguationData":[OSD([subQ0])]}),makeQuery(id+"F18.opExtrude","SWEPT_FACE",FACE,{"disambiguationData":[OSD([subQ0])]})]});}
            var Q4;
            Q4=makeQuery(id+"F17.opExtrude","SWEPT_FACE",FACE,{"disambiguationData":[OSD([sQuery(id+"F16.wireOp",EDGE,"E61.MirrorCS")])]});
            var Q5;
            {var subQ0=sQuery(id+"F16.wireOp",EDGE,"E65.MirrorCS");Q5=makeQuery(id+"F18.boolean.opBoolean","MERGE",FACE,{"derivedFrom":[makeQuery(id+"F17.opExtrude","SWEPT_FACE",FACE,{"disambiguationData":[OSD([subQ0])]}),makeQuery(id+"F18.opExtrude","SWEPT_FACE",FACE,{"disambiguationData":[OSD([subQ0])]})]});}
            var Q6;
            {var subQ0=sQuery(id+"F16.wireOp",EDGE,"E43");Q6=makeQuery(id+"F21.boolean.opBoolean","INTERSECT",EDGE,{"derivedFrom":[makeQuery(id+"F18.boolean.opBoolean","MERGE",FACE,{"derivedFrom":[makeQuery(id+"F17.opExtrude","SWEPT_FACE",FACE,{"disambiguationData":[OSD([subQ0])]}),makeQuery(id+"F18.opExtrude","SWEPT_FACE",FACE,{"disambiguationData":[OSD([subQ0])]})]}),makeQuery(id+"F21.opExtrude","CAP_FACE",FACE,{"disambiguationData":[OSD([sQuery(id+"F20.wireOp",EDGE,"aRbjOPna-xZnc-C8Jd-pmW3-zzcMf3MHO61y.bottom"),sQuery(id+"F20.wireOp",EDGE,"aRbjOPna-xZnc-C8Jd-pmW3-zzcMf3MHO61y.top"),sQuery(id+"F20.wireOp",EDGE,"aRbjOPna-xZnc-C8Jd-pmW3-zzcMf3MHO61y.left"),sQuery(id+"F20.wireOp",EDGE,"aRbjOPna-xZnc-C8Jd-pmW3-zzcMf3MHO61y.right")])],"isStart":true})]});}
            var Q7;
            {var subQ0=sQuery(id+"F16.wireOp",EDGE,"E41");Q7=makeQuery(id+"F21.boolean.opBoolean","INTERSECT",EDGE,{"derivedFrom":[makeQuery(id+"F18.boolean.opBoolean","MERGE",FACE,{"derivedFrom":[makeQuery(id+"F17.opExtrude","SWEPT_FACE",FACE,{"disambiguationData":[OSD([subQ0])]}),makeQuery(id+"F18.opExtrude","SWEPT_FACE",FACE,{"disambiguationData":[OSD([subQ0])]})]}),makeQuery(id+"F21.opExtrude","CAP_FACE",FACE,{"disambiguationData":[OSD([sQuery(id+"F20.wireOp",EDGE,"aRbjOPna-xZnc-C8Jd-pmW3-zzcMf3MHO61y.bottom"),sQuery(id+"F20.wireOp",EDGE,"aRbjOPna-xZnc-C8Jd-pmW3-zzcMf3MHO61y.top"),sQuery(id+"F20.wireOp",EDGE,"aRbjOPna-xZnc-C8Jd-pmW3-zzcMf3MHO61y.left"),sQuery(id+"F20.wireOp",EDGE,"aRbjOPna-xZnc-C8Jd-pmW3-zzcMf3MHO61y.right")])],"isStart":true})]});}
            var Q8;
            Q8=makeQuery(id+"F21.boolean.opBoolean","INTERSECT",EDGE,{"derivedFrom":[makeQuery(id+"F17.opExtrude","SWEPT_FACE",FACE,{"disambiguationData":[OSD([sQuery(id+"F16.wireOp",EDGE,"E45")])]}),makeQuery(id+"F21.opExtrude","CAP_FACE",FACE,{"disambiguationData":[OSD([sQuery(id+"F20.wireOp",EDGE,"aRbjOPna-xZnc-C8Jd-pmW3-zzcMf3MHO61y.bottom"),sQuery(id+"F20.wireOp",EDGE,"aRbjOPna-xZnc-C8Jd-pmW3-zzcMf3MHO61y.top"),sQuery(id+"F20.wireOp",EDGE,"aRbjOPna-xZnc-C8Jd-pmW3-zzcMf3MHO61y.left"),sQuery(id+"F20.wireOp",EDGE,"aRbjOPna-xZnc-C8Jd-pmW3-zzcMf3MHO61y.right")])],"isStart":true})]});
            var Q9;
            Q9=makeQuery(id+"F21.boolean.opBoolean","INTERSECT",EDGE,{"derivedFrom":[makeQuery(id+"F17.opExtrude","SWEPT_FACE",FACE,{"disambiguationData":[OSD([sQuery(id+"F16.wireOp",EDGE,"E49")])]}),makeQuery(id+"F21.opExtrude","CAP_FACE",FACE,{"disambiguationData":[OSD([sQuery(id+"F20.wireOp",EDGE,"aRbjOPna-xZnc-C8Jd-pmW3-zzcMf3MHO61y.bottom"),sQuery(id+"F20.wireOp",EDGE,"aRbjOPna-xZnc-C8Jd-pmW3-zzcMf3MHO61y.top"),sQuery(id+"F20.wireOp",EDGE,"aRbjOPna-xZnc-C8Jd-pmW3-zzcMf3MHO61y.left"),sQuery(id+"F20.wireOp",EDGE,"aRbjOPna-xZnc-C8Jd-pmW3-zzcMf3MHO61y.right")])],"isStart":true})]});
            var Q10;
            Q10=makeQuery(id+"F21.boolean.opBoolean","INTERSECT",EDGE,{"derivedFrom":[makeQuery(id+"F17.opExtrude","SWEPT_FACE",FACE,{"disambiguationData":[OSD([sQuery(id+"F16.wireOp",EDGE,"E75.MirrorCS")])]}),makeQuery(id+"F21.opExtrude","CAP_FACE",FACE,{"disambiguationData":[OSD([sQuery(id+"F20.wireOp",EDGE,"aRbjOPna-xZnc-C8Jd-pmW3-zzcMf3MHO61y.bottom"),sQuery(id+"F20.wireOp",EDGE,"aRbjOPna-xZnc-C8Jd-pmW3-zzcMf3MHO61y.top"),sQuery(id+"F20.wireOp",EDGE,"aRbjOPna-xZnc-C8Jd-pmW3-zzcMf3MHO61y.left"),sQuery(id+"F20.wireOp",EDGE,"aRbjOPna-xZnc-C8Jd-pmW3-zzcMf3MHO61y.right")])],"isStart":true})]});
            var Q11;
            Q11=makeQuery(id+"F21.boolean.opBoolean","INTERSECT",EDGE,{"derivedFrom":[makeQuery(id+"F17.opExtrude","SWEPT_FACE",FACE,{"disambiguationData":[OSD([sQuery(id+"F16.wireOp",EDGE,"E78.MirrorCS")])]}),makeQuery(id+"F21.opExtrude","CAP_FACE",FACE,{"disambiguationData":[OSD([sQuery(id+"F20.wireOp",EDGE,"aRbjOPna-xZnc-C8Jd-pmW3-zzcMf3MHO61y.bottom"),sQuery(id+"F20.wireOp",EDGE,"aRbjOPna-xZnc-C8Jd-pmW3-zzcMf3MHO61y.top"),sQuery(id+"F20.wireOp",EDGE,"aRbjOPna-xZnc-C8Jd-pmW3-zzcMf3MHO61y.left"),sQuery(id+"F20.wireOp",EDGE,"aRbjOPna-xZnc-C8Jd-pmW3-zzcMf3MHO61y.right")])],"isStart":true})]});
            var Q12;
            {var subQ0=sQuery(id+"F16.wireOp",EDGE,"E68.MirrorCS");Q12=makeQuery(id+"F21.boolean.opBoolean","INTERSECT",EDGE,{"derivedFrom":[makeQuery(id+"F18.boolean.opBoolean","MERGE",FACE,{"derivedFrom":[makeQuery(id+"F17.opExtrude","SWEPT_FACE",FACE,{"disambiguationData":[OSD([subQ0])]}),makeQuery(id+"F18.opExtrude","SWEPT_FACE",FACE,{"disambiguationData":[OSD([subQ0])]})]}),makeQuery(id+"F21.opExtrude","CAP_FACE",FACE,{"disambiguationData":[OSD([sQuery(id+"F20.wireOp",EDGE,"aRbjOPna-xZnc-C8Jd-pmW3-zzcMf3MHO61y.bottom"),sQuery(id+"F20.wireOp",EDGE,"aRbjOPna-xZnc-C8Jd-pmW3-zzcMf3MHO61y.top"),sQuery(id+"F20.wireOp",EDGE,"aRbjOPna-xZnc-C8Jd-pmW3-zzcMf3MHO61y.left"),sQuery(id+"F20.wireOp",EDGE,"aRbjOPna-xZnc-C8Jd-pmW3-zzcMf3MHO61y.right")])],"isStart":true})]});}
            var Q13;
            Q13=makeQuery(id+"F21.boolean.opBoolean","INTERSECT",EDGE,{"derivedFrom":[makeQuery(id+"F17.opExtrude","SWEPT_FACE",FACE,{"disambiguationData":[OSD([sQuery(id+"F16.wireOp",EDGE,"E72.MirrorCS")])]}),makeQuery(id+"F21.opExtrude","CAP_FACE",FACE,{"disambiguationData":[OSD([sQuery(id+"F20.wireOp",EDGE,"aRbjOPna-xZnc-C8Jd-pmW3-zzcMf3MHO61y.bottom"),sQuery(id+"F20.wireOp",EDGE,"aRbjOPna-xZnc-C8Jd-pmW3-zzcMf3MHO61y.top"),sQuery(id+"F20.wireOp",EDGE,"aRbjOPna-xZnc-C8Jd-pmW3-zzcMf3MHO61y.left"),sQuery(id+"F20.wireOp",EDGE,"aRbjOPna-xZnc-C8Jd-pmW3-zzcMf3MHO61y.right")])],"isStart":true})]});
            var Q14;
            {var subQ0=sQuery(id+"F16.wireOp",EDGE,"E82.right");var subQ2=sQuery(id+"F16.wireOp",EDGE,"E72.MirrorCS");var subQ4=sQuery(id+"F14.wireOp",EDGE,"E30.top");Q14=makeQuery(id+"F21.boolean.opBoolean","INTERSECT",EDGE,{"derivedFrom":[makeQuery(id+"F17.boolean.opBoolean","SPLIT",FACE,{"disambiguationData":[TD([makeQuery(id+"F15.opExtrude","SWEPT_FACE",FACE,{"disambiguationData":[OSD([subQ4])]})])],"derivedFrom":makeQuery(id+"F17.opExtrude","SWEPT_FACE",FACE,{"disambiguationData":[OSD([subQ0]),TDD([makeQuery(id+"F16.imprint","IMPRINT",EDGE,{"disambiguationData":[TD([[makeQuery(id+"F16.imprint","INTERSECT",VERTEX,{"derivedFrom":[subQ2,subQ0]}),1.0]])],"derivedFrom":subQ0})])]})}),makeQuery(id+"F21.opExtrude","CAP_FACE",FACE,{"disambiguationData":[OSD([sQuery(id+"F20.wireOp",EDGE,"aRbjOPna-xZnc-C8Jd-pmW3-zzcMf3MHO61y.bottom"),sQuery(id+"F20.wireOp",EDGE,"aRbjOPna-xZnc-C8Jd-pmW3-zzcMf3MHO61y.top"),sQuery(id+"F20.wireOp",EDGE,"aRbjOPna-xZnc-C8Jd-pmW3-zzcMf3MHO61y.left"),sQuery(id+"F20.wireOp",EDGE,"aRbjOPna-xZnc-C8Jd-pmW3-zzcMf3MHO61y.right")])],"isStart":true})]});}
            var Q15;
            Q15=makeQuery(id+"F15.opExtrude","CAP_EDGE",EDGE,{"disambiguationData":[OSD([sQuery(id+"F14.wireOp",EDGE,"E30.top")])],"isStart":true});
            var Q16;
            Q16=makeQuery(id+"F15.opExtrude","CAP_EDGE",EDGE,{"disambiguationData":[OSD([sQuery(id+"F14.wireOp",EDGE,"E29.top")])],"isStart":true});
            var Q17;
            {var subQ0=sQuery(id+"F0.wireOp",EDGE,"E0.top");Q17=makeQuery(id+"F2.opShell","OFFSET_EDGE",EDGE,{"disambiguationData":[OSD([subQ0]),TDD([makeQuery(id+"F1.opExtrude","CAP_EDGE",EDGE,{"disambiguationData":[OSD([subQ0])],"isStart":true})])]});}
            var Q18;
            {var subQ0=sQuery(id+"F14.wireOp",EDGE,"E33");Q18=makeQuery(id+"F15.opExtrude","CAP_EDGE",EDGE,{"disambiguationData":[OSD([subQ0]),TDD([makeQuery(id+"F14.imprint","IMPRINT",EDGE,{"disambiguationData":[TD([[makeQuery(id+"F14.imprint","INTERSECT",VERTEX,{"derivedFrom":[sQuery(id+"F14.wireOp",EDGE,"E31.bottom"),subQ0]}),1.0]])],"derivedFrom":subQ0})])],"isStart":true});}
            var Q19;
            {var subQ0=sQuery(id+"F0.wireOp",EDGE,"E0.left");var subQ1=sQuery(id+"F14.wireOp",EDGE,"E29.top");var subQ3=sQuery(id+"F0.wireOp",EDGE,"E0.top");Q19=makeQuery(id+"F15.boolean.opBoolean","SPLIT",EDGE,{"disambiguationData":[TD([makeQuery(id+"F15.opExtrude","SWEPT_FACE",FACE,{"disambiguationData":[OSD([subQ1])]})])],"derivedFrom":makeQuery(id+"F2.opShell","OFFSET_EDGE",EDGE,{"disambiguationData":[OSD([subQ3,subQ0])]})});}
            var Q20;
            {var subQ0=sQuery(id+"F0.wireOp",EDGE,"E0.left");var subQ2=sQuery(id+"F14.wireOp",EDGE,"E30.top");var subQ4=sQuery(id+"F0.wireOp",EDGE,"E0.top");Q20=makeQuery(id+"F15.boolean.opBoolean","SPLIT",EDGE,{"disambiguationData":[TD([makeQuery(id+"F15.opExtrude","SWEPT_FACE",FACE,{"disambiguationData":[OSD([subQ2])]})])],"derivedFrom":makeQuery(id+"F2.opShell","OFFSET_EDGE",EDGE,{"disambiguationData":[OSD([subQ4,subQ0])]})});}
            var Q21;
            {var subQ0=sQuery(id+"F0.wireOp",EDGE,"E0.left");var subQ1=sQuery(id+"F14.wireOp",EDGE,"E33");var subQ2=makeQuery(id+"F15.opExtrude","CAP_FACE",FACE,{"disambiguationData":[OSD([sQuery(id+"F14.wireOp",EDGE,"E29.top"),sQuery(id+"F14.wireOp",EDGE,"E30.top"),sQuery(id+"F14.wireOp",EDGE,"E31.left"),subQ1])],"isStart":true});var subQ3=sQuery(id+"F0.wireOp",EDGE,"E0.right");var subQ4=sQuery(id+"F0.wireOp",EDGE,"E0.top");var subQ5=sQuery(id+"F0.wireOp",EDGE,"E0.bottom");var subQ6=makeQuery(id+"F2.opShell","OFFSET_FACE",FACE,{"disambiguationData":[OSD([subQ5,subQ4,subQ0,subQ3]),TDD([makeQuery(id+"F1.opExtrude","CAP_FACE",FACE,{"disambiguationData":[OSD([subQ5,subQ4,subQ0,subQ3])],"isStart":false})])]});var subQ7=makeQuery(id+"F1.opExtrude","SWEPT_FACE",FACE,{"disambiguationData":[OSD([subQ4])]});var subQ8=makeQuery(id+"F15.opExtrude","CAP_FACE",FACE,{"disambiguationData":[OSD([sQuery(id+"F14.wireOp",EDGE,"E31.bottom"),subQ1,sQuery(id+"F14.wireOp",EDGE,"E34.0"),sQuery(id+"F14.wireOp",EDGE,"E36")])],"isStart":true});Q21=makeQuery(id+"F17.boolean.opBoolean","SPLIT",EDGE,{"disambiguationData":[topologyDisambiguationEdgeConnected([subQ7,subQ6,subQ2,subQ8]),TD([makeQuery(id+"F2.opShell","OFFSET_FACE",FACE,{"disambiguationData":[OSD([subQ0])]})])],"derivedFrom":makeQuery(id+"F2.opShell","OFFSET_EDGE",EDGE,{"disambiguationData":[OSD([subQ4]),TDD([makeQuery(id+"F1.opExtrude","CAP_EDGE",EDGE,{"disambiguationData":[OSD([subQ4])],"isStart":false})])]})});}
            var Q22;
            Q22=makeQuery(id+"F21.boolean.opBoolean","INTERSECT",EDGE,{"derivedFrom":[makeQuery(id+"F17.opExtrude","SWEPT_FACE",FACE,{"disambiguationData":[OSD([sQuery(id+"F16.wireOp",EDGE,"E47")])]}),makeQuery(id+"F21.opExtrude","CAP_FACE",FACE,{"disambiguationData":[OSD([sQuery(id+"F20.wireOp",EDGE,"aRbjOPna-xZnc-C8Jd-pmW3-zzcMf3MHO61y.bottom"),sQuery(id+"F20.wireOp",EDGE,"aRbjOPna-xZnc-C8Jd-pmW3-zzcMf3MHO61y.top"),sQuery(id+"F20.wireOp",EDGE,"aRbjOPna-xZnc-C8Jd-pmW3-zzcMf3MHO61y.left"),sQuery(id+"F20.wireOp",EDGE,"aRbjOPna-xZnc-C8Jd-pmW3-zzcMf3MHO61y.right")])],"isStart":true})]});
            var Q23;
            {var subQ2=sQuery(id+"F14.wireOp",EDGE,"E33");var subQ3=sQuery(id+"F14.wireOp",EDGE,"E31.bottom");var subQ4=sQuery(id+"F16.wireOp",EDGE,"E68.MirrorCS");var subQ5=sQuery(id+"F16.wireOp",EDGE,"E82.right");var subQ6=sQuery(id+"F14.wireOp",EDGE,"E29.top");Q23=makeQuery(id+"F21.boolean.opBoolean","INTERSECT",EDGE,{"derivedFrom":[makeQuery(id+"F18.boolean.opBoolean","SPLIT",FACE,{"disambiguationData":[TD([makeQuery(id+"F15.opExtrude","SWEPT_FACE",FACE,{"disambiguationData":[OSD([subQ6])]})])],"derivedFrom":makeQuery(id+"F17.boolean.opBoolean","MERGE",FACE,{"derivedFrom":[makeQuery(id+"F15.opExtrude","SWEPT_FACE",FACE,{"disambiguationData":[OSD([subQ2]),TDD([makeQuery(id+"F14.imprint","IMPRINT",EDGE,{"disambiguationData":[TD([[makeQuery(id+"F14.imprint","INTERSECT",VERTEX,{"derivedFrom":[subQ3,subQ2]}),1.0]])],"derivedFrom":subQ2})])]}),makeQuery(id+"F17.opExtrude","SWEPT_FACE",FACE,{"disambiguationData":[OSD([subQ5]),TDD([makeQuery(id+"F16.imprint","IMPRINT",EDGE,{"disambiguationData":[TD([[makeQuery(id+"F16.imprint","INTERSECT",VERTEX,{"derivedFrom":[subQ4,subQ5]}),-1.0]])],"derivedFrom":subQ5})])]})]})}),makeQuery(id+"F21.opExtrude","CAP_FACE",FACE,{"disambiguationData":[OSD([sQuery(id+"F20.wireOp",EDGE,"aRbjOPna-xZnc-C8Jd-pmW3-zzcMf3MHO61y.bottom"),sQuery(id+"F20.wireOp",EDGE,"aRbjOPna-xZnc-C8Jd-pmW3-zzcMf3MHO61y.top"),sQuery(id+"F20.wireOp",EDGE,"aRbjOPna-xZnc-C8Jd-pmW3-zzcMf3MHO61y.left"),sQuery(id+"F20.wireOp",EDGE,"aRbjOPna-xZnc-C8Jd-pmW3-zzcMf3MHO61y.right")])],"isStart":true})]});}
            var Q24;
            Q24=makeQuery(id+"F15.opExtrude","CAP_EDGE",EDGE,{"disambiguationData":[OSD([sQuery(id+"F14.wireOp",EDGE,"E36")])],"isStart":true});
            var Q25;
            {var subQ0=sQuery(id+"F16.wireOp",EDGE,"E69.MirrorCS");Q25=makeQuery(id+"F21.boolean.opBoolean","INTERSECT",EDGE,{"derivedFrom":[makeQuery(id+"F18.boolean.opBoolean","MERGE",FACE,{"derivedFrom":[makeQuery(id+"F17.opExtrude","SWEPT_FACE",FACE,{"disambiguationData":[OSD([subQ0])]}),makeQuery(id+"F18.opExtrude","SWEPT_FACE",FACE,{"disambiguationData":[OSD([subQ0])]})]}),makeQuery(id+"F21.opExtrude","CAP_FACE",FACE,{"disambiguationData":[OSD([sQuery(id+"F20.wireOp",EDGE,"aRbjOPna-xZnc-C8Jd-pmW3-zzcMf3MHO61y.bottom"),sQuery(id+"F20.wireOp",EDGE,"aRbjOPna-xZnc-C8Jd-pmW3-zzcMf3MHO61y.top"),sQuery(id+"F20.wireOp",EDGE,"aRbjOPna-xZnc-C8Jd-pmW3-zzcMf3MHO61y.left"),sQuery(id+"F20.wireOp",EDGE,"aRbjOPna-xZnc-C8Jd-pmW3-zzcMf3MHO61y.right")])],"isStart":true})]});}
            var Q26;
            {var subQ0=sQuery(id+"F16.wireOp",EDGE,"E82.top");Q26=makeQuery(id+"F18.boolean.opBoolean","INTERSECT",EDGE,{"derivedFrom":[makeQuery(id+"F9.boolean.opBoolean","MERGE",FACE,{"derivedFrom":[makeQuery(id+"F1.opExtrude","CAP_FACE",FACE,{"disambiguationData":[OSD([sQuery(id+"F0.wireOp",EDGE,"E0.bottom"),sQuery(id+"F0.wireOp",EDGE,"E0.top"),sQuery(id+"F0.wireOp",EDGE,"E0.left"),sQuery(id+"F0.wireOp",EDGE,"E0.right")])],"isStart":false}),makeQuery(id+"F9.opExtrude","SWEPT_FACE",FACE,{"disambiguationData":[OSD([sQuery(id+"F8.wireOp",EDGE,"E9.bottom")])]}),makeQuery(id+"F9.opExtrude","SWEPT_FACE",FACE,{"disambiguationData":[OSD([sQuery(id+"F8.wireOp",EDGE,"E18.MirrorCS")])]})]}),makeQuery(id+"F18.opExtrude","SWEPT_FACE",FACE,{"disambiguationData":[OSD([subQ0]),TDD([makeQuery(id+"F16.imprint","IMPRINT",EDGE,{"disambiguationData":[TD([[makeQuery(id+"F16.imprint","INTERSECT",VERTEX,{"derivedFrom":[sQuery(id+"F16.wireOp",EDGE,"E54"),subQ0]}),1.0]])],"derivedFrom":subQ0})])]})]});}
            var Q27;
            {var subQ0=sQuery(id+"F16.wireOp",EDGE,"E82.top");Q27=makeQuery(id+"F18.boolean.opBoolean","INTERSECT",EDGE,{"derivedFrom":[makeQuery(id+"F9.boolean.opBoolean","MERGE",FACE,{"derivedFrom":[makeQuery(id+"F1.opExtrude","CAP_FACE",FACE,{"disambiguationData":[OSD([sQuery(id+"F0.wireOp",EDGE,"E0.bottom"),sQuery(id+"F0.wireOp",EDGE,"E0.top"),sQuery(id+"F0.wireOp",EDGE,"E0.left"),sQuery(id+"F0.wireOp",EDGE,"E0.right")])],"isStart":false}),makeQuery(id+"F9.opExtrude","SWEPT_FACE",FACE,{"disambiguationData":[OSD([sQuery(id+"F8.wireOp",EDGE,"E9.bottom")])]}),makeQuery(id+"F9.opExtrude","SWEPT_FACE",FACE,{"disambiguationData":[OSD([sQuery(id+"F8.wireOp",EDGE,"E18.MirrorCS")])]})]}),makeQuery(id+"F18.opExtrude","SWEPT_FACE",FACE,{"disambiguationData":[OSD([subQ0]),TDD([makeQuery(id+"F16.imprint","IMPRINT",EDGE,{"disambiguationData":[TD([[makeQuery(id+"F16.imprint","INTERSECT",VERTEX,{"derivedFrom":[sQuery(id+"F16.wireOp",EDGE,"E67.MirrorCS"),subQ0]}),-1.0]])],"derivedFrom":subQ0})])]})]});}
            var Q28;
            {var subQ0=sQuery(id+"F26.wireOp",EDGE,"E104");Q28=makeQuery(id+"F27.boolean.opBoolean","MERGE",EDGE,{"derivedFrom":[makeQuery(id+"F18.boolean.opBoolean","COPY",EDGE,{"derivedFrom":makeQuery(id+"F18.opExtrude","SWEPT_EDGE",EDGE,{"disambiguationData":[OSD([sQuery(id+"F16.wireOp",EDGE,"E54"),sQuery(id+"F16.wireOp",EDGE,"E82.top")])]})}),makeQuery(id+"F27.opExtrude","TWEAK_EDGE",EDGE,{"derivedFrom":[makeQuery(id+"F26.imprint","IMPRINT",EDGE,{"disambiguationData":[TD([[makeQuery(id+"F26.imprint","INTERSECT",VERTEX,{"derivedFrom":[sQuery(id+"F26.wireOp",EDGE,"E103.0"),subQ0]}),1.0]])],"derivedFrom":subQ0}),dummyQuery(id+"F27.vertexPlane.planeOp",FACE)]})]});}
            var Q29;
            {var subQ0=sQuery(id+"F24.wireOp",EDGE,"E100");Q29=makeQuery(id+"F25.boolean.opBoolean","MERGE",EDGE,{"derivedFrom":[makeQuery(id+"F18.boolean.opBoolean","COPY",EDGE,{"derivedFrom":makeQuery(id+"F18.opExtrude","SWEPT_EDGE",EDGE,{"disambiguationData":[OSD([sQuery(id+"F16.wireOp",EDGE,"E67.MirrorCS"),sQuery(id+"F16.wireOp",EDGE,"E82.top")])]})}),makeQuery(id+"F25.opExtrude","TWEAK_EDGE",EDGE,{"derivedFrom":[makeQuery(id+"F24.imprint","IMPRINT",EDGE,{"disambiguationData":[TD([[makeQuery(id+"F24.imprint","INTERSECT",VERTEX,{"derivedFrom":[sQuery(id+"F24.wireOp",EDGE,"E98.0"),subQ0]}),-1.0]])],"derivedFrom":subQ0}),dummyQuery(id+"F25.vertexPlane.planeOp",FACE)]})]});}
            var Q30;
            Q30=makeQuery(id+"F18.boolean.opBoolean","INTERSECT",EDGE,{"derivedFrom":[makeQuery(id+"F9.boolean.opBoolean","MERGE",FACE,{"derivedFrom":[makeQuery(id+"F1.opExtrude","CAP_FACE",FACE,{"disambiguationData":[OSD([sQuery(id+"F0.wireOp",EDGE,"E0.bottom"),sQuery(id+"F0.wireOp",EDGE,"E0.top"),sQuery(id+"F0.wireOp",EDGE,"E0.left"),sQuery(id+"F0.wireOp",EDGE,"E0.right")])],"isStart":false}),makeQuery(id+"F9.opExtrude","SWEPT_FACE",FACE,{"disambiguationData":[OSD([sQuery(id+"F8.wireOp",EDGE,"E9.bottom")])]}),makeQuery(id+"F9.opExtrude","SWEPT_FACE",FACE,{"disambiguationData":[OSD([sQuery(id+"F8.wireOp",EDGE,"E18.MirrorCS")])]})]}),makeQuery(id+"F18.opExtrude","SWEPT_FACE",FACE,{"disambiguationData":[OSD([sQuery(id+"F16.wireOp",EDGE,"E54")])]})]});
            var Q31;
            Q31=makeQuery(id+"F18.boolean.opBoolean","INTERSECT",EDGE,{"derivedFrom":[makeQuery(id+"F9.boolean.opBoolean","MERGE",FACE,{"derivedFrom":[makeQuery(id+"F1.opExtrude","CAP_FACE",FACE,{"disambiguationData":[OSD([sQuery(id+"F0.wireOp",EDGE,"E0.bottom"),sQuery(id+"F0.wireOp",EDGE,"E0.top"),sQuery(id+"F0.wireOp",EDGE,"E0.left"),sQuery(id+"F0.wireOp",EDGE,"E0.right")])],"isStart":false}),makeQuery(id+"F9.opExtrude","SWEPT_FACE",FACE,{"disambiguationData":[OSD([sQuery(id+"F8.wireOp",EDGE,"E9.bottom")])]}),makeQuery(id+"F9.opExtrude","SWEPT_FACE",FACE,{"disambiguationData":[OSD([sQuery(id+"F8.wireOp",EDGE,"E18.MirrorCS")])]})]}),makeQuery(id+"F18.opExtrude","SWEPT_FACE",FACE,{"disambiguationData":[OSD([sQuery(id+"F16.wireOp",EDGE,"E67.MirrorCS")])]})]});
            var Q32;
            Q32=makeQuery(id+"F18.boolean.opBoolean","INTERSECT",EDGE,{"derivedFrom":[makeQuery(id+"F9.boolean.opBoolean","MERGE",FACE,{"derivedFrom":[makeQuery(id+"F1.opExtrude","CAP_FACE",FACE,{"disambiguationData":[OSD([sQuery(id+"F0.wireOp",EDGE,"E0.bottom"),sQuery(id+"F0.wireOp",EDGE,"E0.top"),sQuery(id+"F0.wireOp",EDGE,"E0.left"),sQuery(id+"F0.wireOp",EDGE,"E0.right")])],"isStart":false}),makeQuery(id+"F9.opExtrude","SWEPT_FACE",FACE,{"disambiguationData":[OSD([sQuery(id+"F8.wireOp",EDGE,"E9.bottom")])]}),makeQuery(id+"F9.opExtrude","SWEPT_FACE",FACE,{"disambiguationData":[OSD([sQuery(id+"F8.wireOp",EDGE,"E18.MirrorCS")])]})]}),makeQuery(id+"F18.opExtrude","SWEPT_FACE",FACE,{"disambiguationData":[OSD([sQuery(id+"F16.wireOp",EDGE,"E55"),sQuery(id+"F16.wireOp",EDGE,"E62.MirrorCS")])]})]});
            var Q33;
            {var subQ0=sQuery(id+"F16.wireOp",EDGE,"E82.left");Q33=makeQuery(id+"F18.boolean.opBoolean","INTERSECT",EDGE,{"derivedFrom":[makeQuery(id+"F12.opFillet","BLEND_FACE",FACE,{"disambiguationData":[OSD([sQuery(id+"F0.wireOp",EDGE,"E0.right"),sQuery(id+"F8.wireOp",EDGE,"E17.MirrorCS"),sQuery(id+"F8.wireOp",EDGE,"E18.MirrorCS")])]}),makeQuery(id+"F18.opExtrude","SWEPT_FACE",FACE,{"disambiguationData":[OSD([subQ0]),TDD([makeQuery(id+"F16.imprint","IMPRINT",EDGE,{"disambiguationData":[TD([[makeQuery(id+"F16.imprint","INTERSECT",VERTEX,{"derivedFrom":[sQuery(id+"F16.wireOp",EDGE,"E51"),subQ0]}),-1.0]])],"derivedFrom":subQ0})])]})]});}
            var Q34;
            {var subQ0=sQuery(id+"F16.wireOp",EDGE,"E82.left");var subQ1=sQuery(id+"F16.wireOp",EDGE,"E49");var subQ2=sQuery(id+"F0.wireOp",EDGE,"E0.right");var subQ3=makeQuery(id+"F2.opShell","OFFSET_FACE",FACE,{"disambiguationData":[OSD([subQ2])]});var subQ4=makeQuery(id+"F18.opExtrude","SWEPT_FACE",FACE,{"disambiguationData":[OSD([subQ0]),TDD([makeQuery(id+"F16.imprint","IMPRINT",EDGE,{"disambiguationData":[TD([[makeQuery(id+"F16.imprint","INTERSECT",VERTEX,{"derivedFrom":[sQuery(id+"F16.wireOp",EDGE,"E41"),subQ0]}),1.0]])],"derivedFrom":subQ0})])]});var subQ5=sQuery(id+"F20.wireOp",EDGE,"E89");var subQ6=sQuery(id+"F20.wireOp",EDGE,"E88");var subQ7=sQuery(id+"F20.wireOp",EDGE,"E86.0");var subQ8=makeQuery(id+"F21.opExtrude","CAP_FACE",FACE,{"disambiguationData":[OSD([sQuery(id+"F20.wireOp",EDGE,"E85.0"),subQ7,sQuery(id+"F20.wireOp",EDGE,"E86.1"),sQuery(id+"F20.wireOp",EDGE,"E86.2"),sQuery(id+"F20.wireOp",EDGE,"E87.0"),subQ6,subQ5,sQuery(id+"F20.wireOp",EDGE,"E90"),sQuery(id+"F20.wireOp",EDGE,"E91"),sQuery(id+"F20.wireOp",EDGE,"E92")])],"isStart":true});var subQ9=makeQuery(id+"F18.opExtrude","SWEPT_FACE",FACE,{"disambiguationData":[OSD([subQ0]),TDD([makeQuery(id+"F16.imprint","IMPRINT",EDGE,{"disambiguationData":[TD([[makeQuery(id+"F16.imprint","INTERSECT",VERTEX,{"derivedFrom":[sQuery(id+"F16.wireOp",EDGE,"E43"),subQ0]}),-1.0]])],"derivedFrom":subQ0})])]});var subQ10=makeQuery(id+"F21.opExtrude","SWEPT_FACE",FACE,{"disambiguationData":[OSD([subQ7,subQ6,subQ5])]});Q34=makeQuery(id+"F21.boolean.opBoolean","COPY",EDGE,{"disambiguationData":[topologyDisambiguationEdgeConnected([subQ3,subQ4,subQ9,subQ8,subQ10]),TD([makeQuery(id+"F17.opExtrude","SWEPT_FACE",FACE,{"disambiguationData":[OSD([subQ1])]})])],"derivedFrom":makeQuery(id+"F21.opExtrude","CAP_EDGE",EDGE,{"disambiguationData":[OSD([subQ7,subQ6,subQ5])],"isStart":true})});}
            fillet(context, id + "F28", {"entities" : qUnion([Q0, Q1, Q2, Q3, Q4, Q5, Q6, Q7, Q8, Q9, Q10, Q11, Q12, Q13, Q14, Q15, Q16, Q17, Q18, Q19, Q20, Q21, Q22, Q23, Q24, Q25, Q26, Q27, Q28, Q29, Q30, Q31, Q32, Q33, Q34]), "radius" : .5 * mm, "tangentPropagation" : true, "allowEdgeOverflow" : false});
        }
        {
            var Q0;
            {var subQ2=sQuery(id+"F16.wireOp",EDGE,"E73.MirrorCS");var subQ5=sQuery(id+"F0.wireOp",EDGE,"E0.top");var subQ6=sQuery(id+"F16.wireOp",EDGE,"E82.right");Q0=makeQuery(id+"F21.boolean.opBoolean","INTERSECT",EDGE,{"derivedFrom":[makeQuery(id+"F17.boolean.opBoolean","SPLIT",FACE,{"disambiguationData":[TD([makeQuery(id+"F1.opExtrude","SWEPT_FACE",FACE,{"disambiguationData":[OSD([subQ5])]})])],"derivedFrom":makeQuery(id+"F17.opExtrude","SWEPT_FACE",FACE,{"disambiguationData":[OSD([subQ6]),TDD([makeQuery(id+"F16.imprint","IMPRINT",EDGE,{"disambiguationData":[TD([[makeQuery(id+"F16.imprint","INTERSECT",VERTEX,{"derivedFrom":[subQ2,subQ6]}),1.0]])],"derivedFrom":subQ6})])]})}),makeQuery(id+"F21.opExtrude","CAP_FACE",FACE,{"disambiguationData":[OSD([sQuery(id+"F20.wireOp",EDGE,"aRbjOPna-xZnc-C8Jd-pmW3-zzcMf3MHO61y.bottom"),sQuery(id+"F20.wireOp",EDGE,"aRbjOPna-xZnc-C8Jd-pmW3-zzcMf3MHO61y.top"),sQuery(id+"F20.wireOp",EDGE,"aRbjOPna-xZnc-C8Jd-pmW3-zzcMf3MHO61y.left"),sQuery(id+"F20.wireOp",EDGE,"aRbjOPna-xZnc-C8Jd-pmW3-zzcMf3MHO61y.right")])],"isStart":true})]});}
            var Q1;
            Q1=makeQuery(id+"F18.boolean.opBoolean","COPY",EDGE,{"derivedFrom":makeQuery(id+"F18.opExtrude","SWEPT_EDGE",EDGE,{"disambiguationData":[OSD([sQuery(id+"F16.wireOp",EDGE,"E82.bottom"),sQuery(id+"F16.wireOp",EDGE,"E82.right")])]})});
            var Q2;
            {var subQ0=sQuery(id+"F16.wireOp",EDGE,"E82.right");var subQ1=sQuery(id+"F16.wireOp",EDGE,"E68.MirrorCS");Q2=makeQuery(id+"F18.boolean.opBoolean","MERGE",EDGE,{"derivedFrom":[makeQuery(id+"F17.opExtrude","SWEPT_EDGE",EDGE,{"disambiguationData":[OSD([subQ1,subQ0])]}),makeQuery(id+"F18.opExtrude","SWEPT_EDGE",EDGE,{"disambiguationData":[OSD([subQ1,subQ0])]})]});}
            var Q3;
            {var subQ0=sQuery(id+"F16.wireOp",EDGE,"E72.MirrorCS");var subQ1=sQuery(id+"F16.wireOp",EDGE,"E82.right");Q3=makeQuery(id+"F17.boolean.opBoolean","SPLIT",EDGE,{"disambiguationData":[topologyDisambiguationEdgeConnected([makeQuery(id+"F17.opExtrude","SWEPT_FACE",FACE,{"disambiguationData":[OSD([subQ1]),TDD([makeQuery(id+"F16.imprint","IMPRINT",EDGE,{"disambiguationData":[TD([[makeQuery(id+"F16.imprint","INTERSECT",VERTEX,{"derivedFrom":[subQ0,subQ1]}),1.0]])],"derivedFrom":subQ1})])]})])],"derivedFrom":makeQuery(id+"F17.opExtrude","SWEPT_EDGE",EDGE,{"disambiguationData":[OSD([subQ0,subQ1])]})});}
            var Q4;
            {var subQ0=sQuery(id+"F16.wireOp",EDGE,"E78.MirrorCS");var subQ1=makeQuery(id+"F17.opExtrude","SWEPT_FACE",FACE,{"disambiguationData":[OSD([subQ0])]});var subQ2=sQuery(id+"F16.wireOp",EDGE,"E82.right");var subQ3=sQuery(id+"F16.wireOp",EDGE,"E72.MirrorCS");var subQ5=sQuery(id+"F14.wireOp",EDGE,"E30.top");var subQ6=makeQuery(id+"F17.opExtrude","SWEPT_FACE",FACE,{"disambiguationData":[OSD([subQ2]),TDD([makeQuery(id+"F16.imprint","IMPRINT",EDGE,{"disambiguationData":[TD([[makeQuery(id+"F16.imprint","INTERSECT",VERTEX,{"derivedFrom":[subQ3,subQ2]}),1.0]])],"derivedFrom":subQ2})])]});Q4=makeQuery(id+"F17.boolean.opBoolean","SPLIT",EDGE,{"disambiguationData":[topologyDisambiguationEdgeConnected([subQ1,subQ6]),TD([makeQuery(id+"F15.opExtrude","SWEPT_FACE",FACE,{"disambiguationData":[OSD([subQ5])]})])],"derivedFrom":makeQuery(id+"F17.opExtrude","SWEPT_EDGE",EDGE,{"disambiguationData":[OSD([subQ0,subQ2])]})});}
            var Q5;
            {var subQ0=sQuery(id+"F14.wireOp",EDGE,"E33");Q5=makeQuery(id+"F21.boolean.opBoolean","INTERSECT",EDGE,{"derivedFrom":[makeQuery(id+"F15.boolean.opBoolean","MERGE",FACE,{"derivedFrom":[makeQuery(id+"F1.opExtrude","SWEPT_FACE",FACE,{"disambiguationData":[OSD([sQuery(id+"F0.wireOp",EDGE,"E0.top")])]}),makeQuery(id+"F15.opExtrude","CAP_FACE",FACE,{"disambiguationData":[OSD([sQuery(id+"F14.wireOp",EDGE,"E29.top"),sQuery(id+"F14.wireOp",EDGE,"E30.top"),sQuery(id+"F14.wireOp",EDGE,"E31.left"),subQ0])],"isStart":true}),makeQuery(id+"F15.opExtrude","CAP_FACE",FACE,{"disambiguationData":[OSD([sQuery(id+"F14.wireOp",EDGE,"E31.bottom"),subQ0,sQuery(id+"F14.wireOp",EDGE,"E34.0"),sQuery(id+"F14.wireOp",EDGE,"E36")])],"isStart":true})]}),makeQuery(id+"F21.opExtrude","SWEPT_FACE",FACE,{"disambiguationData":[OSD([sQuery(id+"F20.wireOp",EDGE,"E85.0")])]})]});}
            fillet(context, id + "F29", {"entities" : qUnion([Q0, Q1, Q2, Q3, Q4, Q5]), "radius" : .5 * mm, "tangentPropagation" : true, "allowEdgeOverflow" : false});
        }
        {
            var Q0;
            {var subQ0=sQuery(id+"F14.wireOp",EDGE,"E36");var subQ6=sQuery(id+"F20.wireOp",EDGE,"E85.0");var subQ10=sQuery(id+"F20.wireOp",EDGE,"E89");var subQ11=sQuery(id+"F20.wireOp",EDGE,"E88");var subQ12=sQuery(id+"F20.wireOp",EDGE,"E86.0");Q0=makeQuery(id+"F21.boolean.opBoolean","COPY",FACE,{"disambiguationData":[TD([makeQuery(id+"F15.opExtrude","SWEPT_FACE",FACE,{"disambiguationData":[OSD([subQ0])]})])],"derivedFrom":makeQuery(id+"F21.opExtrude","CAP_FACE",FACE,{"disambiguationData":[OSD([subQ6,subQ12,sQuery(id+"F20.wireOp",EDGE,"E86.1"),sQuery(id+"F20.wireOp",EDGE,"E86.2"),sQuery(id+"F20.wireOp",EDGE,"E87.0"),subQ11,subQ10,sQuery(id+"F20.wireOp",EDGE,"E90"),sQuery(id+"F20.wireOp",EDGE,"E91"),sQuery(id+"F20.wireOp",EDGE,"E92")])],"isStart":true})});}
            var sketch = newSketch(context, id + "F30", { "sketchPlane" : qUnion([Q0])});
            skCircle(sketch, "E105", {"center": v(-16.64, 70.48) * mm, "radius": 9.53 * mm});
            skArc(sketch, "E106", {"start": v(-16.64, 62.23) * mm, "mid": v(-8.77, 67.98) * mm, "end": v(-11.86, 77.22) * mm});
            skLineSegment(sketch, "E107", {"start": v(-16.64, 70.48) * mm, "end": v(-16.64, 78.74) * mm});
            skLineSegment(sketch, "E108", {"start": v(-16.64, 78.74) * mm, "end": v(-16.64, 62.23) * mm});
            skLineSegment(sketch, "E109", {"start": v(-16.64, 78.74) * mm, "end": v(-16.64, 79.22) * mm});
            skLineSegment(sketch, "E110", {"start": v(-15.04, 77.33) * mm, "end": v(-16.64, 79.22) * mm});
            skLineSegment(sketch, "E111", {"start": v(-14.3, 76.45) * mm, "end": v(-13.42, 75.41) * mm});
            skLineSegment(sketch, "E112", {"start": v(-13.42, 75.41) * mm, "end": v(-14.3, 76.45) * mm});
            skArc(sketch, "E113", {"start": v(-14.3, 76.45) * mm, "mid": v(-15.11, 75.72) * mm, "end": v(-15.82, 74.87) * mm});
            skArc(sketch, "E114", {"start": v(-15.04, 77.33) * mm, "mid": v(-15.62, 76.16) * mm, "end": v(-15.82, 74.87) * mm});
            skArc(sketch, "E115", {"start": v(-13.42, 75.41) * mm, "mid": v(-15.54, 72.08) * mm, "end": v(-13.42, 68.75) * mm});
            skArc(sketch, "E116", {"start": v(-14.05, 69.12) * mm, "mid": v(-12.27, 69.05) * mm, "end": v(-10.86, 70.15) * mm});
            skArc(sketch, "E117", {"start": v(-10.86, 70.15) * mm, "mid": v(-10.5, 73.8) * mm, "end": v(-11.86, 77.22) * mm});
            skLineSegment(sketch, "E118.MirrorCS", {"start": v(-18.98, 76.45) * mm, "end": v(-19.86, 75.41) * mm});
            skArc(sketch, "E119.MirrorCS", {"start": v(-18.23, 77.33) * mm, "mid": v(-17.65, 76.16) * mm, "end": v(-17.46, 74.87) * mm});
            skArc(sketch, "E120.MirrorCS", {"start": v(-19.86, 75.41) * mm, "mid": v(-17.73, 72.08) * mm, "end": v(-19.86, 68.75) * mm});
            skLineSegment(sketch, "E121.MirrorCS", {"start": v(-19.86, 75.41) * mm, "end": v(-18.98, 76.45) * mm});
            skLineSegment(sketch, "E122.MirrorCS", {"start": v(-18.23, 77.33) * mm, "end": v(-16.64, 79.22) * mm});
            skArc(sketch, "E123.MirrorCS", {"start": v(-16.64, 62.23) * mm, "mid": v(-24.5, 67.98) * mm, "end": v(-21.41, 77.22) * mm});
            skArc(sketch, "E124.MirrorCS", {"start": v(-18.98, 76.45) * mm, "mid": v(-18.16, 75.72) * mm, "end": v(-17.46, 74.87) * mm});
            skArc(sketch, "E125.MirrorCS", {"start": v(-22.41, 70.15) * mm, "mid": v(-22.77, 73.8) * mm, "end": v(-21.41, 77.22) * mm});
            skArc(sketch, "E126.MirrorCS", {"start": v(-19.23, 69.12) * mm, "mid": v(-21, 69.05) * mm, "end": v(-22.41, 70.15) * mm});
            skPoint(sketch, "E127.0", {"position": v(-26.16, 80) * mm});
            skLineSegment(sketch, "E128", {"start": v(-16.64, 80) * mm, "end": v(-16.64, 70.48) * mm});
            skCircle(sketch, "E129", {"center": v(22.86, 72.32) * mm, "radius": 7.9 * mm});
            skLineSegment(sketch, "E130", {"start": v(24.2, 78) * mm, "end": v(22.86, 79.54) * mm});
            skLineSegment(sketch, "E131", {"start": v(24.83, 77.3) * mm, "end": v(25.5, 76.42) * mm});
            skLineSegment(sketch, "E132", {"start": v(24.83, 77.3) * mm, "end": v(24.03, 76.6) * mm});
            skLineSegment(sketch, "E133", {"start": v(24.03, 76.6) * mm, "end": v(23.53, 75.98) * mm});
            skLineSegment(sketch, "E134", {"start": v(23.53, 75.98) * mm, "end": v(23.63, 76.79) * mm});
            skLineSegment(sketch, "E135", {"start": v(23.63, 76.79) * mm, "end": v(23.95, 77.61) * mm});
            skLineSegment(sketch, "E136", {"start": v(23.95, 77.61) * mm, "end": v(24.2, 78) * mm});
            skLineSegment(sketch, "E137", {"start": v(25.5, 76.42) * mm, "end": v(24.72, 75.73) * mm});
            skLineSegment(sketch, "E138", {"start": v(24.72, 75.73) * mm, "end": v(24.21, 75.1) * mm});
            skLineSegment(sketch, "E139", {"start": v(24.21, 75.1) * mm, "end": v(23.81, 74.24) * mm});
            skLineSegment(sketch, "E140", {"start": v(23.81, 74.24) * mm, "end": v(23.7, 73.31) * mm});
            skLineSegment(sketch, "E141", {"start": v(23.7, 73.31) * mm, "end": v(23.84, 72.73) * mm});
            skLineSegment(sketch, "E142", {"start": v(23.84, 72.73) * mm, "end": v(24.19, 71.9) * mm});
            skLineSegment(sketch, "E143", {"start": v(24.19, 71.9) * mm, "end": v(24.7, 71.32) * mm});
            skLineSegment(sketch, "E144", {"start": v(24.7, 71.32) * mm, "end": v(25.5, 71.02) * mm});
            skLineSegment(sketch, "E145", {"start": v(25.5, 71.02) * mm, "end": v(26.17, 71.02) * mm});
            skLineSegment(sketch, "E146", {"start": v(26.17, 71.02) * mm, "end": v(26.88, 71.27) * mm});
            skLineSegment(sketch, "E147", {"start": v(26.88, 71.27) * mm, "end": v(27.61, 72.02) * mm});
            skLineSegment(sketch, "E148", {"start": v(27.61, 72.02) * mm, "end": v(28.17, 73.3) * mm});
            skLineSegment(sketch, "E149", {"start": v(28.17, 73.3) * mm, "end": v(28.17, 74.42) * mm});
            skLineSegment(sketch, "E150", {"start": v(28.17, 74.42) * mm, "end": v(27.8, 75.99) * mm});
            skLineSegment(sketch, "E151", {"start": v(27.8, 75.99) * mm, "end": v(27.4, 76.93) * mm});
            skLineSegment(sketch, "E152", {"start": v(27.4, 76.93) * mm, "end": v(27.1, 77.4) * mm});
            skLineSegment(sketch, "E153", {"start": v(27.1, 77.4) * mm, "end": v(26.75, 77.98) * mm});
            skArc(sketch, "E154", {"start": v(22.86, 65.45) * mm, "mid": v(29.42, 70.28) * mm, "end": v(26.75, 77.98) * mm});
            skLineSegment(sketch, "E155.MirrorCS", {"start": v(19.55, 71.02) * mm, "end": v(18.84, 71.27) * mm});
            skLineSegment(sketch, "E156.MirrorCS", {"start": v(22.01, 73.31) * mm, "end": v(21.88, 72.73) * mm});
            skLineSegment(sketch, "E157.MirrorCS", {"start": v(18.61, 77.4) * mm, "end": v(18.97, 77.98) * mm});
            skLineSegment(sketch, "E158.MirrorCS", {"start": v(17.92, 75.99) * mm, "end": v(18.32, 76.93) * mm});
            skLineSegment(sketch, "E159.MirrorCS", {"start": v(21.53, 71.9) * mm, "end": v(21.02, 71.32) * mm});
            skLineSegment(sketch, "E160.MirrorCS", {"start": v(20.22, 71.02) * mm, "end": v(19.55, 71.02) * mm});
            skLineSegment(sketch, "E161.MirrorCS", {"start": v(21, 75.73) * mm, "end": v(21.5, 75.1) * mm});
            skLineSegment(sketch, "E162.MirrorCS", {"start": v(22.19, 75.98) * mm, "end": v(22.1, 76.79) * mm});
            skLineSegment(sketch, "E163.MirrorCS", {"start": v(20.9, 77.3) * mm, "end": v(21.7, 76.6) * mm});
            skLineSegment(sketch, "E164.MirrorCS", {"start": v(21.9, 74.24) * mm, "end": v(22.01, 73.31) * mm});
            skLineSegment(sketch, "E165.MirrorCS", {"start": v(18.32, 76.93) * mm, "end": v(18.61, 77.4) * mm});
            skLineSegment(sketch, "E166.MirrorCS", {"start": v(21.7, 76.6) * mm, "end": v(22.19, 75.98) * mm});
            skLineSegment(sketch, "E167.MirrorCS", {"start": v(21.88, 72.73) * mm, "end": v(21.53, 71.9) * mm});
            skLineSegment(sketch, "E168.MirrorCS", {"start": v(21.77, 77.61) * mm, "end": v(21.52, 78) * mm});
            skLineSegment(sketch, "E169.MirrorCS", {"start": v(21.5, 75.1) * mm, "end": v(21.9, 74.24) * mm});
            skLineSegment(sketch, "E170.MirrorCS", {"start": v(22.1, 76.79) * mm, "end": v(21.77, 77.61) * mm});
            skLineSegment(sketch, "E171.MirrorCS", {"start": v(21.02, 71.32) * mm, "end": v(20.22, 71.02) * mm});
            skLineSegment(sketch, "E172.MirrorCS", {"start": v(18.84, 71.27) * mm, "end": v(18.1, 72.02) * mm});
            skLineSegment(sketch, "E173.MirrorCS", {"start": v(20.9, 77.3) * mm, "end": v(20.22, 76.42) * mm});
            skLineSegment(sketch, "E174.MirrorCS", {"start": v(21.52, 78) * mm, "end": v(22.86, 79.54) * mm});
            skArc(sketch, "E175.MirrorCS", {"start": v(22.86, 65.45) * mm, "mid": v(16.3, 70.28) * mm, "end": v(18.97, 77.98) * mm});
            skLineSegment(sketch, "E176.MirrorCS", {"start": v(20.22, 76.42) * mm, "end": v(21, 75.73) * mm});
            skLineSegment(sketch, "E177.MirrorCS", {"start": v(17.55, 73.3) * mm, "end": v(17.55, 74.42) * mm});
            skLineSegment(sketch, "E178.MirrorCS", {"start": v(18.1, 72.02) * mm, "end": v(17.55, 73.3) * mm});
            skLineSegment(sketch, "E179.MirrorCS", {"start": v(17.55, 74.42) * mm, "end": v(17.92, 75.99) * mm});
            skCircle(sketch, "E180", {"center": v(-19.12, 31.84) * mm, "radius": 6.35 * mm});
            skLineSegment(sketch, "E181", {"start": v(-18.03, 36.4) * mm, "end": v(-19.12, 37.65) * mm});
            skLineSegment(sketch, "E182", {"start": v(-17.53, 35.85) * mm, "end": v(-16.98, 35.13) * mm});
            skLineSegment(sketch, "E183", {"start": v(-16.98, 35.13) * mm, "end": v(-17.28, 34.9) * mm});
            skLineSegment(sketch, "E184", {"start": v(-17.28, 34.9) * mm, "end": v(-17.73, 34.45) * mm});
            skLineSegment(sketch, "E185", {"start": v(-17.73, 34.45) * mm, "end": v(-18.04, 34.05) * mm});
            skLineSegment(sketch, "E186", {"start": v(-18.04, 34.05) * mm, "end": v(-18.35, 33.35) * mm});
            skLineSegment(sketch, "E187", {"start": v(-18.35, 33.35) * mm, "end": v(-18.43, 32.6) * mm});
            skLineSegment(sketch, "E188", {"start": v(-18.43, 32.6) * mm, "end": v(-18.36, 32.23) * mm});
            skLineSegment(sketch, "E189", {"start": v(-18.36, 32.23) * mm, "end": v(-18.05, 31.54) * mm});
            skLineSegment(sketch, "E190", {"start": v(-18.05, 31.54) * mm, "end": v(-17.85, 31.22) * mm});
            skLineSegment(sketch, "E191", {"start": v(-17.85, 31.22) * mm, "end": v(-17.42, 30.93) * mm});
            skLineSegment(sketch, "E192", {"start": v(-17.42, 30.93) * mm, "end": v(-16.93, 30.78) * mm});
            skLineSegment(sketch, "E193", {"start": v(-16.93, 30.78) * mm, "end": v(-16.56, 30.78) * mm});
            skLineSegment(sketch, "E194", {"start": v(-16.56, 30.78) * mm, "end": v(-15.94, 30.96) * mm});
            skLineSegment(sketch, "E195", {"start": v(-15.94, 30.96) * mm, "end": v(-15.3, 31.58) * mm});
            skLineSegment(sketch, "E196", {"start": v(-15.3, 31.58) * mm, "end": v(-14.84, 32.62) * mm});
            skLineSegment(sketch, "E197", {"start": v(-14.84, 32.62) * mm, "end": v(-14.84, 33.5) * mm});
            skLineSegment(sketch, "E198", {"start": v(-14.84, 33.5) * mm, "end": v(-15.13, 34.75) * mm});
            skLineSegment(sketch, "E199", {"start": v(-15.13, 34.75) * mm, "end": v(-15.43, 35.45) * mm});
            skLineSegment(sketch, "E200", {"start": v(-15.43, 35.45) * mm, "end": v(-15.72, 36) * mm});
            skLineSegment(sketch, "E201", {"start": v(-15.72, 36) * mm, "end": v(-16.01, 36.42) * mm});
            skLineSegment(sketch, "E202", {"start": v(-17.53, 35.85) * mm, "end": v(-17.74, 35.68) * mm});
            skLineSegment(sketch, "E203", {"start": v(-17.74, 35.68) * mm, "end": v(-18.1, 35.33) * mm});
            skLineSegment(sketch, "E204", {"start": v(-18.1, 35.33) * mm, "end": v(-18.38, 35.06) * mm});
            skLineSegment(sketch, "E205", {"start": v(-18.38, 35.06) * mm, "end": v(-18.6, 34.75) * mm});
            skLineSegment(sketch, "E206", {"start": v(-18.6, 34.75) * mm, "end": v(-18.5, 35.38) * mm});
            skLineSegment(sketch, "E207", {"start": v(-18.5, 35.38) * mm, "end": v(-18.34, 35.85) * mm});
            skLineSegment(sketch, "E208", {"start": v(-18.34, 35.85) * mm, "end": v(-18.2, 36.2) * mm});
            skLineSegment(sketch, "E209", {"start": v(-18.2, 36.2) * mm, "end": v(-18.03, 36.4) * mm});
            skPoint(sketch, "E210.start.orphan", {"position": v(-19.12, 38.2) * mm});
            skLineSegment(sketch, "E211.MirrorCS", {"start": v(-20.4, 31.22) * mm, "end": v(-20.82, 30.93) * mm});
            skLineSegment(sketch, "E212.MirrorCS", {"start": v(-22.8, 35.45) * mm, "end": v(-22.52, 36) * mm});
            skLineSegment(sketch, "E213.MirrorCS", {"start": v(-20.19, 31.54) * mm, "end": v(-20.4, 31.22) * mm});
            skLineSegment(sketch, "E214.MirrorCS", {"start": v(-23.4, 32.62) * mm, "end": v(-23.4, 33.5) * mm});
            skLineSegment(sketch, "E215.MirrorCS", {"start": v(-19.65, 34.75) * mm, "end": v(-19.74, 35.38) * mm});
            skLineSegment(sketch, "E216.MirrorCS", {"start": v(-20.96, 34.9) * mm, "end": v(-20.51, 34.45) * mm});
            skLineSegment(sketch, "E217.MirrorCS", {"start": v(-19.74, 35.38) * mm, "end": v(-19.9, 35.85) * mm});
            skLineSegment(sketch, "E218.MirrorCS", {"start": v(-19.9, 35.85) * mm, "end": v(-20.05, 36.2) * mm});
            skLineSegment(sketch, "E219.MirrorCS", {"start": v(-19.86, 35.06) * mm, "end": v(-19.65, 34.75) * mm});
            skLineSegment(sketch, "E220.MirrorCS", {"start": v(-21.68, 30.78) * mm, "end": v(-22.3, 30.96) * mm});
            skLineSegment(sketch, "E221.MirrorCS", {"start": v(-22.3, 30.96) * mm, "end": v(-22.95, 31.58) * mm});
            skLineSegment(sketch, "E222.MirrorCS", {"start": v(-22.52, 36) * mm, "end": v(-22.23, 36.42) * mm});
            skLineSegment(sketch, "E223.MirrorCS", {"start": v(-23.1, 34.75) * mm, "end": v(-22.8, 35.45) * mm});
            skLineSegment(sketch, "E224.MirrorCS", {"start": v(-20.5, 35.68) * mm, "end": v(-20.14, 35.33) * mm});
            skLineSegment(sketch, "E225.MirrorCS", {"start": v(-20.51, 34.45) * mm, "end": v(-20.2, 34.05) * mm});
            skLineSegment(sketch, "E226.MirrorCS", {"start": v(-20.82, 30.93) * mm, "end": v(-21.3, 30.78) * mm});
            skLineSegment(sketch, "E227.MirrorCS", {"start": v(-21.26, 35.13) * mm, "end": v(-20.96, 34.9) * mm});
            skLineSegment(sketch, "E228.MirrorCS", {"start": v(-20.71, 35.85) * mm, "end": v(-20.5, 35.68) * mm});
            skLineSegment(sketch, "E229.MirrorCS", {"start": v(-19.88, 32.23) * mm, "end": v(-20.19, 31.54) * mm});
            skLineSegment(sketch, "E230.MirrorCS", {"start": v(-20.71, 35.85) * mm, "end": v(-21.26, 35.13) * mm});
            skLineSegment(sketch, "E231.MirrorCS", {"start": v(-19.81, 32.6) * mm, "end": v(-19.88, 32.23) * mm});
            skLineSegment(sketch, "E232.MirrorCS", {"start": v(-20.2, 34.05) * mm, "end": v(-19.9, 33.35) * mm});
            skLineSegment(sketch, "E233.MirrorCS", {"start": v(-19.9, 33.35) * mm, "end": v(-19.81, 32.6) * mm});
            skLineSegment(sketch, "E234.MirrorCS", {"start": v(-20.14, 35.33) * mm, "end": v(-19.86, 35.06) * mm});
            skLineSegment(sketch, "E235.MirrorCS", {"start": v(-20.05, 36.2) * mm, "end": v(-20.21, 36.4) * mm});
            skLineSegment(sketch, "E236.MirrorCS", {"start": v(-21.3, 30.78) * mm, "end": v(-21.68, 30.78) * mm});
            skLineSegment(sketch, "E237.MirrorCS", {"start": v(-23.4, 33.5) * mm, "end": v(-23.1, 34.75) * mm});
            skLineSegment(sketch, "E238.MirrorCS", {"start": v(-20.21, 36.4) * mm, "end": v(-19.12, 37.65) * mm});
            skLineSegment(sketch, "E239.MirrorCS", {"start": v(-22.95, 31.58) * mm, "end": v(-23.4, 32.62) * mm});
            skArc(sketch, "E240", {"start": v(-22.23, 36.42) * mm, "mid": v(-19.12, 26.3) * mm, "end": v(-16.01, 36.42) * mm});
            skSolve(sketch);
        }
        {
            var Q0;
            {var subQ0=sQuery(id+"F14.wireOp",EDGE,"E36");var subQ6=sQuery(id+"F20.wireOp",EDGE,"E85.0");var subQ10=sQuery(id+"F20.wireOp",EDGE,"E89");var subQ11=sQuery(id+"F20.wireOp",EDGE,"E88");var subQ12=sQuery(id+"F20.wireOp",EDGE,"E86.0");Q0=makeQuery(id+"F21.boolean.opBoolean","COPY",FACE,{"disambiguationData":[TD([makeQuery(id+"F15.opExtrude","SWEPT_FACE",FACE,{"disambiguationData":[OSD([subQ0])]})])],"derivedFrom":makeQuery(id+"F21.opExtrude","CAP_FACE",FACE,{"disambiguationData":[OSD([subQ6,subQ12,sQuery(id+"F20.wireOp",EDGE,"E86.1"),sQuery(id+"F20.wireOp",EDGE,"E86.2"),sQuery(id+"F20.wireOp",EDGE,"E87.0"),subQ11,subQ10,sQuery(id+"F20.wireOp",EDGE,"E90"),sQuery(id+"F20.wireOp",EDGE,"E91"),sQuery(id+"F20.wireOp",EDGE,"E92")])],"isStart":true})});}
            var sketch = newSketch(context, id + "F31", { "sketchPlane" : qUnion([Q0])});
            skText(sketch, "E241", { "text": "T-70", "fontName": "OpenSans-Bold.ttf"});
            skText(sketch, "E242", { "text": "X-Wing", "fontName": "OpenSans-Bold.ttf"});
            skLineSegment(sketch, "E243", {"start": v(-0.63, 25.92) * mm, "end": v(-0.63, 27.82) * mm});
            skPoint(sketch, "E244", {"position": v(15.43, 19.37) * mm});
            const initialGuessF31  = {"E241": [-0.00893, 0.02782, 1, 0, 0.00576], "E242": [-0.0167, 0.01937, 1, 0, 0.00654]};
            skSetInitialGuess(sketch, initialGuessF31);
            skSolve(sketch);
        }
        {
            var Q0;
            Q0=qSketchRegion(id+"F31",true);
            var Q1;
            Q1=makeQuery(id+"F30.imprint","IMPRINT",FACE,{"disambiguationData":[TD([[makeQuery(id+"F30.imprint","IMPRINT",EDGE,{"derivedFrom":sQuery(id+"F30.wireOp",EDGE,"E182")}),-1.0]])]});
            extrude(context, id + "F32", {"entities" : qUnion([Q0, Q1]), "operationType" : NewBodyOperationType.ADD, "depth" : .5 * mm, "offsetDistance" : 25.4 * mm});
        }
    });
